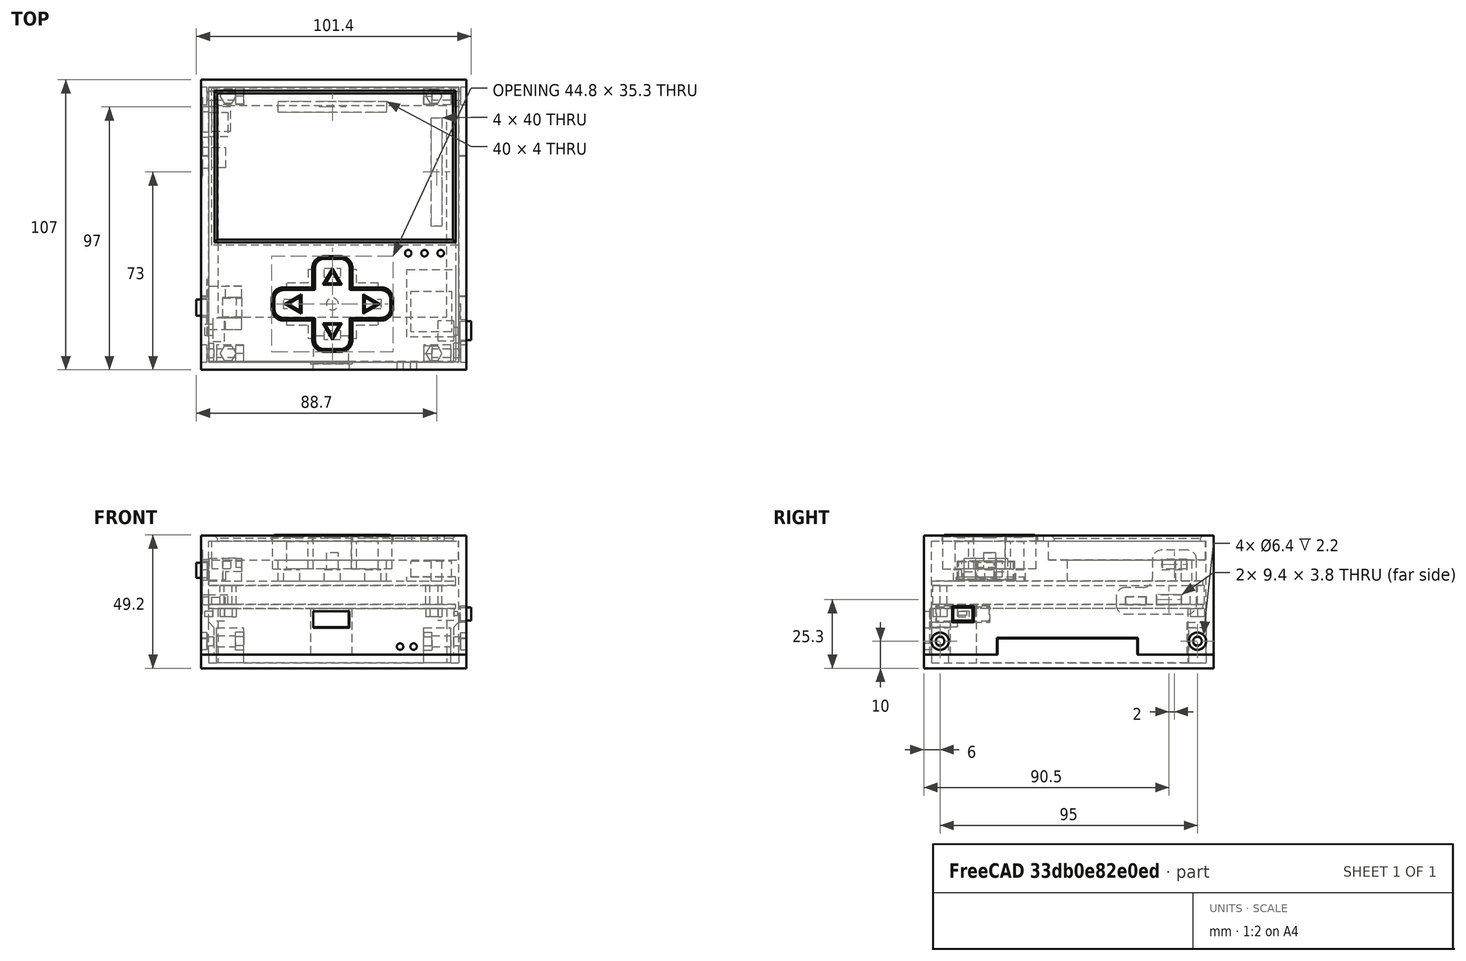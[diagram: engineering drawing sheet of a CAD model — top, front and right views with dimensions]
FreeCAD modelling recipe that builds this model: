
FCSTD DOCUMENT  (FreeCAD 0.19R24276 (Git))
Label: Cube-Vario
License: All rights reserved
LicenseURL: http://en.wikipedia.org/wiki/All_rights_reserved
objects: Sketcher::SketchObject×59, PartDesign::Pad×33, PartDesign::Pocket×23, PartDesign::ShapeBinder×8, PartDesign::Body×8, Mesh::Feature×6, PartDesign::Chamfer×3, PartDesign::Fillet×1
note: 195 computed .brp shape members not serialized (recipe doc carries the construction recipe); baked Part::Feature solids carry a one-line shape summary decoded from their .brp

FEATURE [Sketcher::SketchObject] Sketch
  FullyConstrained = true
  MapMode = 5
  Support = -> [XY_Plane]
  sketch-geometry (20):
    g0: LineSegment StartX=-45.5 StartY=50 StartZ=0 EndX=45.5 EndY=50 EndZ=0
    g1: LineSegment StartX=45.5 StartY=50 StartZ=0 EndX=45.5 EndY=-50 EndZ=0
    g2: LineSegment StartX=45.5 StartY=-50 StartZ=0 EndX=-45.5 EndY=-50 EndZ=0
    g3: LineSegment StartX=-45.5 StartY=-50 StartZ=0 EndX=-45.5 EndY=50 EndZ=0
    g4: LineSegment StartX=-42.2 StartY=44.4 StartZ=0 EndX=42.2 EndY=44.4 EndZ=0
    g5: LineSegment StartX=42.2 StartY=44.4 StartZ=0 EndX=42.2 EndY=-33.6 EndZ=0
    g6: LineSegment StartX=42.2 StartY=-33.6 StartZ=0 EndX=-42.2 EndY=-33.6 EndZ=0
    g7: LineSegment StartX=-42.2 StartY=-33.6 StartZ=0 EndX=-42.2 EndY=44.4 EndZ=0
    g8: LineSegment StartX=-44.1 StartY=-34 StartZ=0 EndX=-39.8 EndY=-34 EndZ=0
    g9: LineSegment StartX=-39.8 StartY=-34 StartZ=0 EndX=-39.8 EndY=-42.6 EndZ=0
    g10: LineSegment StartX=-39.8 StartY=-42.6 StartZ=0 EndX=-44.1 EndY=-42.6 EndZ=0
    g11: LineSegment StartX=-44.1 StartY=-42.6 StartZ=0 EndX=-44.1 EndY=-34 EndZ=0
    g12: LineSegment StartX=-7 StartY=-40.6 StartZ=0 EndX=6 EndY=-40.6 EndZ=0
    g13: LineSegment StartX=6 StartY=-40.6 StartZ=0 EndX=6 EndY=-50.6 EndZ=0
    g14: LineSegment StartX=6 StartY=-50.6 StartZ=0 EndX=-7 EndY=-50.6 EndZ=0
    g15: LineSegment StartX=-7 StartY=-50.6 StartZ=0 EndX=-7 EndY=-40.6 EndZ=0
    g16: LineSegment StartX=38.9 StartY=-35 StartZ=0 EndX=44.9 EndY=-35 EndZ=0
    g17: LineSegment StartX=44.9 StartY=-35 StartZ=0 EndX=44.9 EndY=-42.4 EndZ=0
    g18: LineSegment StartX=44.9 StartY=-42.4 StartZ=0 EndX=38.9 EndY=-42.4 EndZ=0
    g19: LineSegment StartX=38.9 StartY=-42.4 StartZ=0 EndX=38.9 EndY=-35 EndZ=0
  constraints (57):
    c: Coincident(g0,g1)
    c: Coincident(g1,g2)
    c: Coincident(g2,g3)
    c: Coincident(g3,g0)
    c: Horizontal(g2)
    c: Vertical(g3)
    c: DistanceX(g0,g0) = 91
    c: DistanceY(g3,g3) = 100
    c: Symmetric(g0,g0,g-2)
    c: Symmetric(g0,g1,g-1)
    c: Coincident(g4,g5)
    c: Coincident(g5,g6)
    c: Coincident(g6,g7)
    c: Coincident(g7,g4)
    c: Horizontal(g6)
    c: Vertical(g7)
    c: Coincident(g8,g9)
    c: Coincident(g9,g10)
    c: Coincident(g10,g11)
    c: Coincident(g11,g8)
    c: Horizontal(g8)
    c: Horizontal(g10)
    c: Vertical(g9)
    c: Vertical(g11)
    c: Coincident(g12,g13)
    c: Coincident(g13,g14)
    c: Coincident(g14,g15)
    c: Coincident(g15,g12)
    c: Horizontal(g12)
    c: Horizontal(g14)
    c: Vertical(g13)
    c: Vertical(g15)
    c: Coincident(g16,g17)
    c: Coincident(g17,g18)
    c: Coincident(g18,g19)
    c: Coincident(g19,g16)
    c: Horizontal(g16)
    c: Horizontal(g18)
    c: Vertical(g17)
    c: Vertical(g19)
    c: DistanceY(g4,g0) = 5.6
    c: DistanceY(g7,g7) = 78
    c: DistanceX(g4,g4) = 84.4
    c: Symmetric(g4,g4,g-2)
    c: Vertical(g5)
    c: DistanceY(g11,g11) = 8.6
    c: DistanceY(g17,g17) = 7.4
    c: DistanceX(g10,g10) = 4.3
    c: DistanceX(g14,g14) = 13
    c: DistanceY(g13,g13) = 10
    c: DistanceX(g2,g14) = 38.5
    c: DistanceX(g18,g18) = 6
    c: DistanceY(g1,g16) = 15
    c: DistanceY(g2,g8) = 16
    c: DistanceY(g13,g1) = 0.6
    c: DistanceX(g2,g10) = 1.4
    c: DistanceX(g18,g1) = 6.6
FEATURE [PartDesign::ShapeBinder] ShapeBinder
  Support = -> [Sketch]
  TraceSupport = false
FEATURE [Sketcher::SketchObject] Sketch001
  ExternalGeometry = -> [ShapeBinder]
  FullyConstrained = true
  MapMode = 5
  Support = -> [XY_Plane001]
  sketch-geometry (4):
    g0: LineSegment StartX=-45.5 StartY=50 StartZ=0 EndX=45.5 EndY=50 EndZ=0
    g1: LineSegment StartX=45.5 StartY=50 StartZ=0 EndX=45.5 EndY=-50 EndZ=0
    g2: LineSegment StartX=45.5 StartY=-50 StartZ=0 EndX=-45.5 EndY=-50 EndZ=0
    g3: LineSegment StartX=-45.5 StartY=-50 StartZ=0 EndX=-45.5 EndY=50 EndZ=0
  constraints (10):
    c: Coincident(g0,g1)
    c: Coincident(g1,g2)
    c: Coincident(g2,g3)
    c: Coincident(g3,g0)
    c: Horizontal(g0)
    c: Horizontal(g2)
    c: Vertical(g1)
    c: Vertical(g3)
    c: Coincident(g0,g-3)
    c: Coincident(g1,g-4)
FEATURE [PartDesign::Pad] Pad
  Direction = (1,1,1)
  Length = 1.6
  Length2 = 100
  Profile = -> Sketch001
  Type = 0
FEATURE [Sketcher::SketchObject] Sketch002
  ExternalGeometry = -> [ShapeBinder]
  FullyConstrained = true
  MapMode = 5
  Placement = pos=(0,0,0) rot=(1,0,0;3.14159rad)
  Support = -> [Pad]
  sketch-geometry (4):
    g0: LineSegment StartX=-42.2 StartY=33.6 StartZ=0 EndX=42.2 EndY=33.6 EndZ=0
    g1: LineSegment StartX=42.2 StartY=33.6 StartZ=0 EndX=42.2 EndY=-44.4 EndZ=0
    g2: LineSegment StartX=42.2 StartY=-44.4 StartZ=0 EndX=-42.2 EndY=-44.4 EndZ=0
    g3: LineSegment StartX=-42.2 StartY=-44.4 StartZ=0 EndX=-42.2 EndY=33.6 EndZ=0
  constraints (10):
    c: Coincident(g0,g1)
    c: Coincident(g1,g2)
    c: Coincident(g2,g3)
    c: Coincident(g3,g0)
    c: Horizontal(g0)
    c: Horizontal(g2)
    c: Vertical(g1)
    c: Vertical(g3)
    c: Coincident(g0,g-3)
    c: Coincident(g1,g-4)
FEATURE [PartDesign::Pad] Pad001
  BaseFeature = -> Pad
  Direction = (1,1,1)
  Length = 20
  Length2 = 100
  Profile = -> Sketch002
  Type = 0
FEATURE [Sketcher::SketchObject] Sketch003
  ExternalGeometry = -> [ShapeBinder]
  FullyConstrained = true
  MapMode = 5
  Placement = pos=(0,0,0) rot=(1,0,0;3.14159rad)
  Support = -> [Pad001]
  sketch-geometry (4):
    g0: LineSegment StartX=-7 StartY=50.6 StartZ=0 EndX=6 EndY=50.6 EndZ=0
    g1: LineSegment StartX=6 StartY=50.6 StartZ=0 EndX=6 EndY=40.6 EndZ=0
    g2: LineSegment StartX=6 StartY=40.6 StartZ=0 EndX=-7 EndY=40.6 EndZ=0
    g3: LineSegment StartX=-7 StartY=40.6 StartZ=0 EndX=-7 EndY=50.6 EndZ=0
  constraints (10):
    c: Coincident(g0,g1)
    c: Coincident(g1,g2)
    c: Coincident(g2,g3)
    c: Coincident(g3,g0)
    c: Horizontal(g0)
    c: Horizontal(g2)
    c: Vertical(g1)
    c: Vertical(g3)
    c: Coincident(g0,g-3)
    c: Coincident(g1,g-4)
FEATURE [PartDesign::Pad] Pad002
  BaseFeature = -> Pad001
  Direction = (1,1,1)
  Length = 6.8
  Length2 = 100
  Profile = -> Sketch003
  Type = 0
FEATURE [Sketcher::SketchObject] Sketch004
  ExternalGeometry = -> [ShapeBinder]
  FullyConstrained = true
  MapMode = 5
  Placement = pos=(0,0,0) rot=(1,0,0;3.14159rad)
  Support = -> [Pad002]
  sketch-geometry (4):
    g0: LineSegment StartX=-44.1 StartY=42.6 StartZ=0 EndX=-39.8 EndY=42.6 EndZ=0
    g1: LineSegment StartX=-39.8 StartY=42.6 StartZ=0 EndX=-39.8 EndY=34 EndZ=0
    g2: LineSegment StartX=-39.8 StartY=34 StartZ=0 EndX=-44.1 EndY=34 EndZ=0
    g3: LineSegment StartX=-44.1 StartY=34 StartZ=0 EndX=-44.1 EndY=42.6 EndZ=0
  constraints (10):
    c: Coincident(g0,g1)
    c: Coincident(g1,g2)
    c: Coincident(g2,g3)
    c: Coincident(g3,g0)
    c: Horizontal(g0)
    c: Horizontal(g2)
    c: Vertical(g1)
    c: Vertical(g3)
    c: Coincident(g0,g-3)
    c: Coincident(g1,g-4)
FEATURE [PartDesign::Pad] Pad003
  BaseFeature = -> Pad002
  Direction = (1,1,1)
  Length = 4.6
  Length2 = 100
  Profile = -> Sketch004
  Type = 0
FEATURE [Sketcher::SketchObject] Sketch005
  ExternalGeometry = -> [ShapeBinder]
  FullyConstrained = true
  MapMode = 5
  Placement = pos=(0,0,0) rot=(1,0,0;3.14159rad)
  Support = -> [Pad003]
  sketch-geometry (4):
    g0: LineSegment StartX=38.9 StartY=42.4 StartZ=0 EndX=44.9 EndY=42.4 EndZ=0
    g1: LineSegment StartX=44.9 StartY=42.4 StartZ=0 EndX=44.9 EndY=35 EndZ=0
    g2: LineSegment StartX=44.9 StartY=35 StartZ=0 EndX=38.9 EndY=35 EndZ=0
    g3: LineSegment StartX=38.9 StartY=35 StartZ=0 EndX=38.9 EndY=42.4 EndZ=0
  constraints (10):
    c: Coincident(g0,g1)
    c: Coincident(g1,g2)
    c: Coincident(g2,g3)
    c: Coincident(g3,g0)
    c: Horizontal(g0)
    c: Horizontal(g2)
    c: Vertical(g1)
    c: Vertical(g3)
    c: Coincident(g0,g-3)
    c: Coincident(g1,g-4)
FEATURE [PartDesign::Pad] Pad004
  BaseFeature = -> Pad003
  Direction = (1,1,1)
  Length = 4.4
  Length2 = 100
  Profile = -> Sketch005
  Type = 0
FEATURE [Sketcher::SketchObject] Sketch006
  ExternalGeometry = -> [Pad004]
  FullyConstrained = true
  MapMode = 5
  Placement = pos=(-44.1,0,0) rot=(0.57735,-0.57735,-0.57735;2.0944rad)
  Support = -> [Pad004]
  sketch-geometry (4):
    g0: LineSegment StartX=36.2 StartY=-1 StartZ=0 EndX=40.4 EndY=-1 EndZ=0
    g1: LineSegment StartX=40.4 StartY=-1 StartZ=0 EndX=40.4 EndY=-3 EndZ=0
    g2: LineSegment StartX=40.4 StartY=-3 StartZ=0 EndX=36.2 EndY=-3 EndZ=0
    g3: LineSegment StartX=36.2 StartY=-3 StartZ=0 EndX=36.2 EndY=-1 EndZ=0
  constraints (12):
    c: Coincident(g0,g1)
    c: Coincident(g1,g2)
    c: Coincident(g2,g3)
    c: Coincident(g3,g0)
    c: Horizontal(g0)
    c: Horizontal(g2)
    c: Vertical(g1)
    c: Vertical(g3)
    c: DistanceX(g0,g-4) = 2.2
    c: DistanceY(g3,g3) = 2
    c: DistanceX(g0,g0) = 4.2
    c: DistanceY(g0,g-3) = 1
FEATURE [PartDesign::Pad] Pad005
  BaseFeature = -> Pad004
  Direction = (1,1,1)
  Length = 3
  Length2 = 100
  Profile = -> Sketch006
  Type = 0
FEATURE [Sketcher::SketchObject] Sketch007
  ExternalGeometry = -> [Pad005]
  FullyConstrained = true
  MapMode = 5
  Placement = pos=(44.9,0,0) rot=(0.57735,0.57735,0.57735;2.0944rad)
  Support = -> [Pad005]
  sketch-geometry (4):
    g0: LineSegment StartX=-40.2 StartY=-1 StartZ=0 EndX=-37.2 EndY=-1 EndZ=0
    g1: LineSegment StartX=-37.2 StartY=-1 StartZ=0 EndX=-37.2 EndY=-2.5 EndZ=0
    g2: LineSegment StartX=-37.2 StartY=-2.5 StartZ=0 EndX=-40.2 EndY=-2.5 EndZ=0
    g3: LineSegment StartX=-40.2 StartY=-2.5 StartZ=0 EndX=-40.2 EndY=-1 EndZ=0
  constraints (12):
    c: Coincident(g0,g1)
    c: Coincident(g1,g2)
    c: Coincident(g2,g3)
    c: Coincident(g3,g0)
    c: Horizontal(g0)
    c: Horizontal(g2)
    c: Vertical(g1)
    c: Vertical(g3)
    c: DistanceX(g0,g0) = 3
    c: DistanceX(g0,g-4) = 2.2
    c: DistanceY(g3,g3) = 1.5
    c: DistanceY(g0,g-3) = 1
FEATURE [PartDesign::Pad] Pad006
  BaseFeature = -> Pad005
  Direction = (1,1,1)
  Length = 1.4
  Length2 = 100
  Profile = -> Sketch007
  Type = 0
FEATURE [Sketcher::SketchObject] Sketch008
  ExternalGeometry = -> [Pad006]
  FullyConstrained = true
  MapMode = 5
  Placement = pos=(0,0,1.6) rot=(0,0,1;0rad)
  Support = -> [Pad006]
  sketch-geometry (28):
    g0: LineSegment StartX=-40 StartY=45.4019 StartZ=0 EndX=-37 EndY=45.4019 EndZ=0
    g1: LineSegment StartX=-37 StartY=45.4019 StartZ=0 EndX=-35.5 EndY=48 EndZ=0
    g2: LineSegment StartX=-35.5 StartY=48 StartZ=0 EndX=-37 EndY=50.5981 EndZ=0
    g3: LineSegment StartX=-37 StartY=50.5981 StartZ=0 EndX=-40 EndY=50.5981 EndZ=0
    g4: LineSegment StartX=-40 StartY=50.5981 StartZ=0 EndX=-41.5 EndY=48 EndZ=0
    g5: LineSegment StartX=-41.5 StartY=48 StartZ=0 EndX=-40 EndY=45.4019 EndZ=0
    g6: Circle CenterX=-38.5 CenterY=48 CenterZ=0 NormalX=0 NormalY=0 NormalZ=1 AngleXU=0 Radius=3
    g7: LineSegment StartX=39 StartY=45.4019 StartZ=0 EndX=40.5 EndY=48 EndZ=0
    g8: LineSegment StartX=40.5 StartY=48 StartZ=0 EndX=39 EndY=50.5981 EndZ=0
    g9: LineSegment StartX=39 StartY=50.5981 StartZ=0 EndX=36 EndY=50.5981 EndZ=0
    g10: LineSegment StartX=36 StartY=50.5981 StartZ=0 EndX=34.5 EndY=48 EndZ=0
    g11: LineSegment StartX=34.5 StartY=48 StartZ=0 EndX=36 EndY=45.4019 EndZ=0
    g12: LineSegment StartX=36 StartY=45.4019 StartZ=0 EndX=39 EndY=45.4019 EndZ=0
    g13: Circle CenterX=37.5 CenterY=48 CenterZ=0 NormalX=0 NormalY=0 NormalZ=1 AngleXU=0 Radius=3
    g14: LineSegment StartX=-37 StartY=-49.5981 StartZ=0 EndX=-35.5 EndY=-47 EndZ=0
    g15: LineSegment StartX=-35.5 StartY=-47 StartZ=0 EndX=-37 EndY=-44.4019 EndZ=0
    g16: LineSegment StartX=-37 StartY=-44.4019 StartZ=0 EndX=-40 EndY=-44.4019 EndZ=0
    g17: LineSegment StartX=-40 StartY=-44.4019 StartZ=0 EndX=-41.5 EndY=-47 EndZ=0
    g18: LineSegment StartX=-41.5 StartY=-47 StartZ=0 EndX=-40 EndY=-49.5981 EndZ=0
    g19: LineSegment StartX=-40 StartY=-49.5981 StartZ=0 EndX=-37 EndY=-49.5981 EndZ=0
    g20: Circle CenterX=-38.5 CenterY=-47 CenterZ=0 NormalX=0 NormalY=0 NormalZ=1 AngleXU=0 Radius=3
    g21: LineSegment StartX=39 StartY=-49.5981 StartZ=0 EndX=40.5 EndY=-47 EndZ=0
    g22: LineSegment StartX=40.5 StartY=-47 StartZ=0 EndX=39 EndY=-44.4019 EndZ=0
    g23: LineSegment StartX=39 StartY=-44.4019 StartZ=0 EndX=36 EndY=-44.4019 EndZ=0
    g24: LineSegment StartX=36 StartY=-44.4019 StartZ=0 EndX=34.5 EndY=-47 EndZ=0
    g25: LineSegment StartX=34.5 StartY=-47 StartZ=0 EndX=36 EndY=-49.5981 EndZ=0
    g26: LineSegment StartX=36 StartY=-49.5981 StartZ=0 EndX=39 EndY=-49.5981 EndZ=0
    g27: Circle CenterX=37.5 CenterY=-47 CenterZ=0 NormalX=0 NormalY=0 NormalZ=1 AngleXU=0 Radius=3
  constraints (68):
    c: Coincident(g0,g1)
    c: Coincident(g1,g2)
    c: Coincident(g2,g3)
    c: Coincident(g3,g4)
    c: Coincident(g4,g5)
    c: Coincident(g5,g0)
    c: Equal(g0, g1-g5) x5
    c: PointOnObject(g0,g6)
    c: PointOnObject(g1,g6)
    c: PointOnObject(g2,g6)
    c: PointOnObject(g3,g6)
    c: PointOnObject(g4,g6)
    c: PointOnObject(g5,g6)
    c: Coincident(g7,g8)
    c: Coincident(g8,g9)
    c: Coincident(g9,g10)
    c: Coincident(g10,g11)
    c: Coincident(g11,g12)
    c: Coincident(g12,g7)
    c: Equal(g7, g8-g12) x5
    c: PointOnObject(g7,g13)
    c: PointOnObject(g8,g13)
    c: PointOnObject(g9,g13)
    c: PointOnObject(g10,g13)
    c: PointOnObject(g11,g13)
    c: PointOnObject(g12,g13)
    c: Coincident(g14,g15)
    c: Coincident(g15,g16)
    c: Coincident(g16,g17)
    c: Coincident(g17,g18)
    c: Coincident(g18,g19)
    c: Coincident(g19,g14)
    c: Equal(g14, g15-g19) x5
    c: PointOnObject(g14,g20)
    c: PointOnObject(g15,g20)
    c: PointOnObject(g16,g20)
    c: PointOnObject(g17,g20)
    c: PointOnObject(g18,g20)
    c: PointOnObject(g19,g20)
    c: Coincident(g21,g22)
    c: Coincident(g22,g23)
    c: Coincident(g23,g24)
    c: Coincident(g24,g25)
    c: Coincident(g25,g26)
    c: Coincident(g26,g21)
    c: Equal(g21, g22-g26) x5
    c: PointOnObject(g21,g27)
    c: PointOnObject(g22,g27)
    c: PointOnObject(g23,g27)
    c: PointOnObject(g24,g27)
    c: PointOnObject(g25,g27)
    c: PointOnObject(g26,g27)
    c: Equal(g20,g27)
    c: Radius(g27) = 3
    c: Horizontal(g17,g14)
    c: Horizontal(g24,g21)
    c: Horizontal(g4,g1)
    c: Horizontal(g10,g7)
    c: Equal(g20,g6)
    c: Equal(g6,g13)
    c: Horizontal(g6,g13)
    c: Horizontal(g20,g27)
    c: DistanceY(g6,g-3) = 2
    c: DistanceY(g-3,g20) = 3
    c: Vertical(g6,g20)
    c: DistanceX(g-3,g6) = 7
    c: Vertical(g13,g27)
    c: DistanceX(g13,g-4) = 8
FEATURE [PartDesign::Pad] Pad007
  BaseFeature = -> Pad006
  Direction = (1,1,1)
  Length = 7
  Length2 = 100
  Profile = -> Sketch008
  Type = 0
FEATURE [Sketcher::SketchObject] Sketch009
  ExternalGeometry = -> [Pad007]
  FullyConstrained = true
  MapMode = 5
  Placement = pos=(0,0,1.6) rot=(0,0,1;0rad)
  Support = -> [Pad007]
  sketch-geometry (4):
    g0: LineSegment StartX=-45.5 StartY=42 StartZ=0 EndX=-38.5 EndY=42 EndZ=0
    g1: LineSegment StartX=-38.5 StartY=42 StartZ=0 EndX=-38.5 EndY=33 EndZ=0
    g2: LineSegment StartX=-38.5 StartY=33 StartZ=0 EndX=-45.5 EndY=33 EndZ=0
    g3: LineSegment StartX=-45.5 StartY=33 StartZ=0 EndX=-45.5 EndY=42 EndZ=0
  constraints (12):
    c: Coincident(g0,g1)
    c: Coincident(g1,g2)
    c: Coincident(g2,g3)
    c: Coincident(g3,g0)
    c: Horizontal(g0)
    c: Horizontal(g2)
    c: Vertical(g1)
    c: Vertical(g3)
    c: PointOnObject(g0,g-3)
    c: DistanceX(g0,g0) = 7
    c: DistanceY(g3,g3) = 9
    c: DistanceY(g0,g-3) = 8
FEATURE [PartDesign::Pad] Pad008
  BaseFeature = -> Pad007
  Direction = (1,1,1)
  Length = 3.4
  Length2 = 100
  Profile = -> Sketch009
  Type = 0
FEATURE [Sketcher::SketchObject] Sketch010
  ExternalGeometry = -> [Pad008]
  FullyConstrained = true
  MapMode = 5
  Placement = pos=(0,0,1.6) rot=(0,0,1;0rad)
  Support = -> [Pad008]
  sketch-geometry (4):
    g0: LineSegment StartX=-44.5 StartY=29 StartZ=0 EndX=-39.5 EndY=29 EndZ=0
    g1: LineSegment StartX=-39.5 StartY=29 StartZ=0 EndX=-39.5 EndY=21.6 EndZ=0
    g2: LineSegment StartX=-39.5 StartY=21.6 StartZ=0 EndX=-44.5 EndY=21.6 EndZ=0
    g3: LineSegment StartX=-44.5 StartY=21.6 StartZ=0 EndX=-44.5 EndY=29 EndZ=0
  constraints (12):
    c: Coincident(g0,g1)
    c: Coincident(g1,g2)
    c: Coincident(g2,g3)
    c: Coincident(g3,g0)
    c: Horizontal(g0)
    c: Horizontal(g2)
    c: Vertical(g1)
    c: Vertical(g3)
    c: DistanceX(g0,g0) = 5
    c: DistanceY(g3,g3) = 7.4
    c: DistanceY(g0,g-4) = 21
    c: DistanceX(g-4,g0) = 1
FEATURE [PartDesign::Pad] Pad009
  BaseFeature = -> Pad008
  Direction = (1,1,1)
  Length = 2.6
  Length2 = 100
  Profile = -> Sketch010
  Type = 0
FEATURE [Sketcher::SketchObject] Sketch011
  ExternalGeometry = -> [Pad009]
  FullyConstrained = true
  MapMode = 5
  Placement = pos=(0,0,8.6) rot=(0,0,1;0rad)
  Support = -> [Pad009]
  sketch-geometry (4):
    g0: LineSegment StartX=-45.5 StartY=50 StartZ=0 EndX=45.5 EndY=50 EndZ=0
    g1: LineSegment StartX=45.5 StartY=50 StartZ=0 EndX=45.5 EndY=-50 EndZ=0
    g2: LineSegment StartX=45.5 StartY=-50 StartZ=0 EndX=-45.5 EndY=-50 EndZ=0
    g3: LineSegment StartX=-45.5 StartY=-50 StartZ=0 EndX=-45.5 EndY=50 EndZ=0
  constraints (10):
    c: Coincident(g0,g1)
    c: Coincident(g1,g2)
    c: Coincident(g2,g3)
    c: Coincident(g3,g0)
    c: Horizontal(g0)
    c: Horizontal(g2)
    c: Vertical(g1)
    c: Vertical(g3)
    c: Coincident(g0,g-3)
    c: Coincident(g1,g-4)
FEATURE [PartDesign::Pad] Pad010
  BaseFeature = -> Pad009
  Direction = (1,1,1)
  Length = 1.6
  Length2 = 100
  Profile = -> Sketch011
  Type = 0
FEATURE [Sketcher::SketchObject] Sketch012
  ExternalGeometry = -> [Pad010]
  FullyConstrained = true
  MapMode = 5
  Placement = pos=(0,0,10.2) rot=(0,0,1;0rad)
  Support = -> [Pad010]
  sketch-geometry (8):
    g0: LineSegment StartX=-20 StartY=46 StartZ=0 EndX=20 EndY=46 EndZ=0
    g1: LineSegment StartX=20 StartY=46 StartZ=0 EndX=20 EndY=42 EndZ=0
    g2: LineSegment StartX=20 StartY=42 StartZ=0 EndX=-20 EndY=42 EndZ=0
    g3: LineSegment StartX=-20 StartY=42 StartZ=0 EndX=-20 EndY=46 EndZ=0
    g4: LineSegment StartX=36.5 StartY=40 StartZ=0 EndX=40.5 EndY=40 EndZ=0
    g5: LineSegment StartX=40.5 StartY=40 StartZ=0 EndX=40.5 EndY=5.1941e-12 EndZ=0
    g6: LineSegment StartX=40.5 StartY=5.1941e-12 StartZ=0 EndX=36.5 EndY=5.1941e-12 EndZ=0
    g7: LineSegment StartX=36.5 StartY=5.1941e-12 StartZ=0 EndX=36.5 EndY=40 EndZ=0
  constraints (23):
    c: Coincident(g0,g1)
    c: Coincident(g1,g2)
    c: Coincident(g2,g3)
    c: Coincident(g3,g0)
    c: Horizontal(g2)
    c: Vertical(g1)
    c: Vertical(g3)
    c: Coincident(g4,g5)
    c: Coincident(g5,g6)
    c: Coincident(g6,g7)
    c: Coincident(g7,g4)
    c: Horizontal(g4)
    c: Horizontal(g6)
    c: Vertical(g5)
    c: Vertical(g7)
    c: Equal(g1,g4)
    c: Equal(g2,g7)
    c: Symmetric(g0,g0,g-2)
    c: DistanceX(g0,g0) = 40
    c: DistanceY(g3,g3) = 4
    c: DistanceX(g4,g-3) = 5
    c: DistanceY(g4,g2) = 2
    c: DistanceY(g0,g-3) = 4
FEATURE [PartDesign::Pad] Pad011
  BaseFeature = -> Pad010
  Direction = (1,1,1)
  Length = 7.8
  Length2 = 100
  Profile = -> Sketch012
  Type = 0
FEATURE [Sketcher::SketchObject] Sketch013
  ExternalGeometry = -> [Pad011]
  FullyConstrained = true
  MapMode = 5
  Placement = pos=(0,0,18) rot=(0,0,1;0rad)
  Support = -> [Pad011]
  sketch-geometry (4):
    g0: LineSegment StartX=-44.5 StartY=51 StartZ=0 EndX=46.5 EndY=51 EndZ=0
    g1: LineSegment StartX=46.5 StartY=51 StartZ=0 EndX=46.5 EndY=-7 EndZ=0
    g2: LineSegment StartX=46.5 StartY=-7 StartZ=0 EndX=-44.5 EndY=-7 EndZ=0
    g3: LineSegment StartX=-44.5 StartY=-7 StartZ=0 EndX=-44.5 EndY=51 EndZ=0
  constraints (12):
    c: Coincident(g0,g1)
    c: Coincident(g1,g2)
    c: Coincident(g2,g3)
    c: Coincident(g3,g0)
    c: Horizontal(g0)
    c: Horizontal(g2)
    c: Vertical(g1)
    c: Vertical(g3)
    c: DistanceY(g3,g3) = 58
    c: DistanceX(g0,g0) = 91
    c: DistanceX(g-3,g0) = 1
    c: DistanceY(g-3,g0) = 1
FEATURE [PartDesign::Pad] Pad012
  BaseFeature = -> Pad011
  Direction = (1,1,1)
  Length = 7
  Length2 = 100
  Profile = -> Sketch013
  Type = 0
FEATURE [Sketcher::SketchObject] Sketch014
  ExternalGeometry = -> [Pad012]
  FullyConstrained = true
  MapMode = 5
  Placement = pos=(0,0,18) rot=(1,0,0;3.14159rad)
  Support = -> [Pad012]
  sketch-geometry (4):
    g0: LineSegment StartX=-44.5 StartY=-35 StartZ=0 EndX=-37.5 EndY=-35 EndZ=0
    g1: LineSegment StartX=-37.5 StartY=-35 StartZ=0 EndX=-37.5 EndY=-44 EndZ=0
    g2: LineSegment StartX=-37.5 StartY=-44 StartZ=0 EndX=-44.5 EndY=-44 EndZ=0
    g3: LineSegment StartX=-44.5 StartY=-44 StartZ=0 EndX=-44.5 EndY=-35 EndZ=0
  constraints (12):
    c: Coincident(g0,g1)
    c: Coincident(g1,g2)
    c: Coincident(g2,g3)
    c: Coincident(g3,g0)
    c: Horizontal(g0)
    c: Horizontal(g2)
    c: Vertical(g1)
    c: Vertical(g3)
    c: PointOnObject(g0,g-3)
    c: DistanceX(g0,g0) = 7
    c: DistanceY(g3,g3) = 9
    c: DistanceY(g-3,g2) = 7
FEATURE [PartDesign::Pad] Pad013
  BaseFeature = -> Pad012
  Direction = (1,1,1)
  Length = 3.4
  Length2 = 100
  Profile = -> Sketch014
  Type = 0
FEATURE [Sketcher::SketchObject] Sketch015
  ExternalGeometry = -> [Pad013]
  FullyConstrained = true
  MapMode = 5
  Placement = pos=(0,0,0) rot=(1,0,0;3.14159rad)
  Support = -> [Pad013]
  sketch-geometry (28):
    g0: LineSegment StartX=-35.5 StartY=47 StartZ=0 EndX=-37 EndY=49.5981 EndZ=0
    g1: LineSegment StartX=-37 StartY=49.5981 StartZ=0 EndX=-40 EndY=49.5981 EndZ=0
    g2: LineSegment StartX=-40 StartY=49.5981 StartZ=0 EndX=-41.5 EndY=47 EndZ=0
    g3: LineSegment StartX=-41.5 StartY=47 StartZ=0 EndX=-40 EndY=44.4019 EndZ=0
    g4: LineSegment StartX=-40 StartY=44.4019 StartZ=0 EndX=-37 EndY=44.4019 EndZ=0
    g5: LineSegment StartX=-37 StartY=44.4019 StartZ=0 EndX=-35.5 EndY=47 EndZ=0
    g6: Circle CenterX=-38.5 CenterY=47 CenterZ=0 NormalX=0 NormalY=0 NormalZ=1 AngleXU=0 Radius=3
    g7: LineSegment StartX=39 StartY=44.4019 StartZ=0 EndX=40.5 EndY=47 EndZ=0
    g8: LineSegment StartX=40.5 StartY=47 StartZ=0 EndX=39 EndY=49.5981 EndZ=0
    g9: LineSegment StartX=39 StartY=49.5981 StartZ=0 EndX=36 EndY=49.5981 EndZ=0
    g10: LineSegment StartX=36 StartY=49.5981 StartZ=0 EndX=34.5 EndY=47 EndZ=0
    g11: LineSegment StartX=34.5 StartY=47 StartZ=0 EndX=36 EndY=44.4019 EndZ=0
    g12: LineSegment StartX=36 StartY=44.4019 StartZ=0 EndX=39 EndY=44.4019 EndZ=0
    g13: Circle CenterX=37.5 CenterY=47 CenterZ=0 NormalX=0 NormalY=0 NormalZ=1 AngleXU=0 Radius=3
    g14: LineSegment StartX=-37 StartY=-50.5981 StartZ=0 EndX=-35.5 EndY=-48 EndZ=0
    g15: LineSegment StartX=-35.5 StartY=-48 StartZ=0 EndX=-37 EndY=-45.4019 EndZ=0
    g16: LineSegment StartX=-37 StartY=-45.4019 StartZ=0 EndX=-40 EndY=-45.4019 EndZ=0
    g17: LineSegment StartX=-40 StartY=-45.4019 StartZ=0 EndX=-41.5 EndY=-48 EndZ=0
    g18: LineSegment StartX=-41.5 StartY=-48 StartZ=0 EndX=-40 EndY=-50.5981 EndZ=0
    g19: LineSegment StartX=-40 StartY=-50.5981 StartZ=0 EndX=-37 EndY=-50.5981 EndZ=0
    g20: Circle CenterX=-38.5 CenterY=-48 CenterZ=0 NormalX=0 NormalY=0 NormalZ=1 AngleXU=0 Radius=3
    g21: LineSegment StartX=39 StartY=-50.5981 StartZ=0 EndX=40.5 EndY=-48 EndZ=0
    g22: LineSegment StartX=40.5 StartY=-48 StartZ=0 EndX=39 EndY=-45.4019 EndZ=0
    g23: LineSegment StartX=39 StartY=-45.4019 StartZ=0 EndX=36 EndY=-45.4019 EndZ=0
    g24: LineSegment StartX=36 StartY=-45.4019 StartZ=0 EndX=34.5 EndY=-48 EndZ=0
    g25: LineSegment StartX=34.5 StartY=-48 StartZ=0 EndX=36 EndY=-50.5981 EndZ=0
    g26: LineSegment StartX=36 StartY=-50.5981 StartZ=0 EndX=39 EndY=-50.5981 EndZ=0
    g27: Circle CenterX=37.5 CenterY=-48 CenterZ=0 NormalX=0 NormalY=0 NormalZ=1 AngleXU=0 Radius=3
  constraints (64):
    c: Coincident(g0,g1)
    c: Coincident(g1,g2)
    c: Coincident(g2,g3)
    c: Coincident(g3,g4)
    c: Coincident(g4,g5)
    c: Coincident(g5,g0)
    c: Equal(g0, g1-g5) x5
    c: PointOnObject(g0,g6)
    c: PointOnObject(g1,g6)
    c: PointOnObject(g2,g6)
    c: PointOnObject(g3,g6)
    c: PointOnObject(g4,g6)
    c: PointOnObject(g5,g6)
    c: Coincident(g7,g8)
    c: Coincident(g8,g9)
    c: Coincident(g9,g10)
    c: Coincident(g10,g11)
    c: Coincident(g11,g12)
    c: Coincident(g12,g7)
    c: Equal(g7, g8-g12) x5
    c: PointOnObject(g7,g13)
    c: PointOnObject(g8,g13)
    c: PointOnObject(g9,g13)
    c: PointOnObject(g10,g13)
    c: PointOnObject(g11,g13)
    c: PointOnObject(g12,g13)
    c: Coincident(g14,g15)
    c: Coincident(g15,g16)
    c: Coincident(g16,g17)
    c: Coincident(g17,g18)
    c: Coincident(g18,g19)
    c: Coincident(g19,g14)
    c: Equal(g14, g15-g19) x5
    c: PointOnObject(g14,g20)
    c: PointOnObject(g15,g20)
    c: PointOnObject(g16,g20)
    c: PointOnObject(g17,g20)
    c: PointOnObject(g18,g20)
    c: PointOnObject(g19,g20)
    c: Coincident(g21,g22)
    c: Coincident(g22,g23)
    c: Coincident(g23,g24)
    c: Coincident(g24,g25)
    c: Coincident(g25,g26)
    c: Coincident(g26,g21)
    c: Equal(g21, g22-g26) x5
    c: PointOnObject(g21,g27)
    c: PointOnObject(g22,g27)
    c: PointOnObject(g23,g27)
    c: PointOnObject(g24,g27)
    c: PointOnObject(g25,g27)
    c: PointOnObject(g26,g27)
    c: Equal(g6,g13)
    c: Equal(g13,g20)
    c: Equal(g20,g27)
    c: Radius(g27) = 3
    c: Horizontal(g21,g24)
    c: Coincident(g21,g-10)
    c: Horizontal(g14,g17)
    c: Coincident(g17,g-7)
    c: Horizontal(g0,g2)
    c: Coincident(g2,g-3)
    c: Horizontal(g10,g7)
    c: Coincident(g7,g-6)
FEATURE [PartDesign::Pad] Pad014
  BaseFeature = -> Pad013
  Direction = (1,1,1)
  Length = 3
  Length2 = 100
  Profile = -> Sketch015
  Type = 0
FEATURE [PartDesign::ShapeBinder] ShapeBinder001
  Support = -> [Sketch]
  TraceSupport = false
FEATURE [PartDesign::ShapeBinder] ShapeBinder002
  Support = -> [Sketch]
  TraceSupport = false
FEATURE [Sketcher::SketchObject] Sketch016
  FullyConstrained = true
  MapMode = 5
  Placement = pos=(0,0,0) rot=(0.57735,0.57735,0.57735;2.0944rad)
  Support = -> [YZ_Plane]
  sketch-geometry (14):
    g0: LineSegment StartX=-44.4019 StartY=-13.5 StartZ=0 EndX=-44.4019 EndY=-10.5 EndZ=0
    g1: LineSegment StartX=-44.4019 StartY=-10.5 StartZ=0 EndX=-47 EndY=-9 EndZ=0
    g2: LineSegment StartX=-47 StartY=-9 StartZ=0 EndX=-49.5981 EndY=-10.5 EndZ=0
    g3: LineSegment StartX=-49.5981 StartY=-10.5 StartZ=0 EndX=-49.5981 EndY=-13.5 EndZ=0
    g4: LineSegment StartX=-49.5981 StartY=-13.5 StartZ=0 EndX=-47 EndY=-15 EndZ=0
    g5: LineSegment StartX=-47 StartY=-15 StartZ=0 EndX=-44.4019 EndY=-13.5 EndZ=0
    g6: Circle CenterX=-47 CenterY=-12 CenterZ=0 NormalX=0 NormalY=0 NormalZ=1 AngleXU=0 Radius=3
    g7: LineSegment StartX=50.5981 StartY=-10.5 StartZ=0 EndX=48 EndY=-9 EndZ=0
    g8: LineSegment StartX=48 StartY=-9 StartZ=0 EndX=45.4019 EndY=-10.5 EndZ=0
    g9: LineSegment StartX=45.4019 StartY=-10.5 StartZ=0 EndX=45.4019 EndY=-13.5 EndZ=0
    g10: LineSegment StartX=45.4019 StartY=-13.5 StartZ=0 EndX=48 EndY=-15 EndZ=0
    g11: LineSegment StartX=48 StartY=-15 StartZ=0 EndX=50.5981 EndY=-13.5 EndZ=0
    g12: LineSegment StartX=50.5981 StartY=-13.5 StartZ=0 EndX=50.5981 EndY=-10.5 EndZ=0
    g13: Circle CenterX=48 CenterY=-12 CenterZ=0 NormalX=0 NormalY=0 NormalZ=1 AngleXU=0 Radius=3
  constraints (34):
    c: Coincident(g0,g1)
    c: Coincident(g1,g2)
    c: Coincident(g2,g3)
    c: Coincident(g3,g4)
    c: Coincident(g4,g5)
    c: Coincident(g5,g0)
    c: Equal(g0, g1-g5) x5
    c: PointOnObject(g0,g6)
    c: PointOnObject(g1,g6)
    c: PointOnObject(g2,g6)
    c: PointOnObject(g3,g6)
    c: PointOnObject(g4,g6)
    c: PointOnObject(g5,g6)
    c: Coincident(g7,g8)
    c: Coincident(g8,g9)
    c: Coincident(g9,g10)
    c: Coincident(g10,g11)
    c: Coincident(g11,g12)
    c: Coincident(g12,g7)
    c: Equal(g7, g8-g12) x5
    c: PointOnObject(g7,g13)
    c: PointOnObject(g8,g13)
    c: PointOnObject(g9,g13)
    c: PointOnObject(g10,g13)
    c: PointOnObject(g11,g13)
    c: PointOnObject(g12,g13)
    c: Equal(g6,g13)
    c: Radius(g13) = 3
    c: Vertical(g1,g4)
    c: Vertical(g10,g7)
    c: DistanceX(g-1,g13) = 48
    c: DistanceY(g6,g-1) = 12
    c: DistanceX(g6,g-1) = 47
    c: Horizontal(g6,g13)
FEATURE [PartDesign::ShapeBinder] ShapeBinder003
  Support = -> [Sketch016]
  TraceSupport = false
FEATURE [PartDesign::ShapeBinder] ShapeBinder004
  Support = -> [Sketch016,ShapeBinder003]
  TraceSupport = false
FEATURE [Sketcher::SketchObject] Sketch017
  AttachmentOffset = pos=(0,0,-22) rot=(0,0,1;0rad)
  ExternalGeometry = -> [ShapeBinder001]
  FullyConstrained = true
  MapMode = 5
  Placement = pos=(0,0,-22) rot=(0,0,1;0rad)
  Support = -> [XY_Plane002]
  sketch-geometry (4):
    g0: LineSegment StartX=-48.5 StartY=54 StartZ=0 EndX=49.5 EndY=54 EndZ=0
    g1: LineSegment StartX=49.5 StartY=54 StartZ=0 EndX=49.5 EndY=-53 EndZ=0
    g2: LineSegment StartX=49.5 StartY=-53 StartZ=0 EndX=-48.5 EndY=-53 EndZ=0
    g3: LineSegment StartX=-48.5 StartY=-53 StartZ=0 EndX=-48.5 EndY=54 EndZ=0
  constraints (12):
    c: Coincident(g0,g1)
    c: Coincident(g1,g2)
    c: Coincident(g2,g3)
    c: Coincident(g3,g0)
    c: Horizontal(g0)
    c: Horizontal(g2)
    c: Vertical(g1)
    c: Vertical(g3)
    c: DistanceX(g0,g-3) = 3
    c: DistanceX(g-5,g0) = 4
    c: DistanceY(g-3,g0) = 4
    c: DistanceY(g2,g-6) = 3
FEATURE [PartDesign::Pad] Pad015
  Direction = (1,1,1)
  Length = 5
  Length2 = 100
  Profile = -> Sketch017
  Type = 0
FEATURE [Sketcher::SketchObject] Sketch018
  ExternalGeometry = -> [ShapeBinder001]
  FullyConstrained = true
  MapMode = 5
  Placement = pos=(0,0,-17) rot=(0,0,1;0rad)
  Support = -> [Pad015]
  sketch-geometry (4):
    g0: LineSegment StartX=-45.7 StartY=51.2 StartZ=0 EndX=46.7 EndY=51.2 EndZ=0
    g1: LineSegment StartX=46.7 StartY=51.2 StartZ=0 EndX=46.7 EndY=-50.2 EndZ=0
    g2: LineSegment StartX=46.7 StartY=-50.2 StartZ=0 EndX=-45.7 EndY=-50.2 EndZ=0
    g3: LineSegment StartX=-45.7 StartY=-50.2 StartZ=0 EndX=-45.7 EndY=51.2 EndZ=0
  constraints (12):
    c: Coincident(g0,g1)
    c: Coincident(g1,g2)
    c: Coincident(g2,g3)
    c: Coincident(g3,g0)
    c: Horizontal(g0)
    c: Horizontal(g2)
    c: Vertical(g1)
    c: Vertical(g3)
    c: DistanceX(g0,g-3) = 0.2
    c: DistanceY(g-3,g0) = 1.2
    c: DistanceX(g-4,g1) = 1.2
    c: DistanceY(g1,g-4) = 0.2
FEATURE [PartDesign::Pocket] Pocket
  BaseFeature = -> Pad015
  Length = 3
  Length2 = 100
  Profile = -> Sketch018
  Type = 0
FEATURE [Sketcher::SketchObject] Sketch019
  ExternalGeometry = -> [Pocket]
  FullyConstrained = true
  MapMode = 5
  Placement = pos=(0,0,-17) rot=(0,0,1;0rad)
  Support = -> [Pocket]
  sketch-geometry (8):
    g0: LineSegment StartX=-48.5 StartY=25.8 StartZ=0 EndX=-45.7 EndY=25.8 EndZ=0
    g1: LineSegment StartX=-45.7 StartY=25.8 StartZ=0 EndX=-45.7 EndY=-25.8 EndZ=0
    g2: LineSegment StartX=-45.7 StartY=-25.8 StartZ=0 EndX=-48.5 EndY=-25.8 EndZ=0
    g3: LineSegment StartX=-48.5 StartY=-25.8 StartZ=0 EndX=-48.5 EndY=25.8 EndZ=0
    g4: LineSegment StartX=46.7 StartY=25.8 StartZ=0 EndX=49.5 EndY=25.8 EndZ=0
    g5: LineSegment StartX=49.5 StartY=25.8 StartZ=0 EndX=49.5 EndY=-25.8 EndZ=0
    g6: LineSegment StartX=49.5 StartY=-25.8 StartZ=0 EndX=46.7 EndY=-25.8 EndZ=0
    g7: LineSegment StartX=46.7 StartY=-25.8 StartZ=0 EndX=46.7 EndY=25.8 EndZ=0
  constraints (23):
    c: Coincident(g0,g1)
    c: Coincident(g1,g2)
    c: Coincident(g2,g3)
    c: Coincident(g3,g0)
    c: Horizontal(g0)
    c: Horizontal(g2)
    c: Vertical(g1)
    c: PointOnObject(g0,g-3)
    c: PointOnObject(g1,g-4)
    c: Coincident(g4,g5)
    c: Coincident(g5,g6)
    c: Coincident(g6,g7)
    c: Coincident(g7,g4)
    c: Horizontal(g4)
    c: Horizontal(g6)
    c: Vertical(g5)
    c: Vertical(g7)
    c: PointOnObject(g4,g-5)
    c: PointOnObject(g5,g-6)
    c: Equal(g1,g7)
    c: Horizontal(g0,g4)
    c: Symmetric(g0,g2,g-1)
    c: DistanceY(g-1,g0) = 25.8
FEATURE [PartDesign::Pad] Pad016
  BaseFeature = -> Pocket
  Direction = (1,1,1)
  Length = 6
  Length2 = 100
  Profile = -> Sketch019
  Type = 0
FEATURE [Sketcher::SketchObject] Sketch020
  ExternalGeometry = -> [Pad016]
  FullyConstrained = true
  MapMode = 5
  Placement = pos=(0,0,-20) rot=(0,0,1;0rad)
  Support = -> [Pad016]
  sketch-geometry (16):
    g0: LineSegment StartX=-42.7 StartY=51.2 StartZ=0 EndX=-32.7 EndY=51.2 EndZ=0
    g1: LineSegment StartX=-32.7 StartY=51.2 StartZ=0 EndX=-32.7 EndY=44.8 EndZ=0
    g2: LineSegment StartX=-32.7 StartY=44.8 StartZ=0 EndX=-42.7 EndY=44.8 EndZ=0
    g3: LineSegment StartX=-42.7 StartY=44.8 StartZ=0 EndX=-42.7 EndY=51.2 EndZ=0
    g4: LineSegment StartX=33.7 StartY=51.2 StartZ=0 EndX=43.7 EndY=51.2 EndZ=0
    g5: LineSegment StartX=43.7 StartY=51.2 StartZ=0 EndX=43.7 EndY=44.8 EndZ=0
    g6: LineSegment StartX=43.7 StartY=44.8 StartZ=0 EndX=33.7 EndY=44.8 EndZ=0
    g7: LineSegment StartX=33.7 StartY=44.8 StartZ=0 EndX=33.7 EndY=51.2 EndZ=0
    g8: LineSegment StartX=-42.7 StartY=-50.2 StartZ=0 EndX=-32.7 EndY=-50.2 EndZ=0
    g9: LineSegment StartX=-32.7 StartY=-50.2 StartZ=0 EndX=-32.7 EndY=-43.8 EndZ=0
    g10: LineSegment StartX=-32.7 StartY=-43.8 StartZ=0 EndX=-42.7 EndY=-43.8 EndZ=0
    g11: LineSegment StartX=-42.7 StartY=-43.8 StartZ=0 EndX=-42.7 EndY=-50.2 EndZ=0
    g12: LineSegment StartX=33.7 StartY=-50.2 StartZ=0 EndX=43.7 EndY=-50.2 EndZ=0
    g13: LineSegment StartX=43.7 StartY=-50.2 StartZ=0 EndX=43.7 EndY=-43.8 EndZ=0
    g14: LineSegment StartX=43.7 StartY=-43.8 StartZ=0 EndX=33.7 EndY=-43.8 EndZ=0
    g15: LineSegment StartX=33.7 StartY=-43.8 StartZ=0 EndX=33.7 EndY=-50.2 EndZ=0
  constraints (48):
    c: Coincident(g0,g1)
    c: Coincident(g1,g2)
    c: Coincident(g2,g3)
    c: Coincident(g3,g0)
    c: Horizontal(g0)
    c: Horizontal(g2)
    c: Vertical(g1)
    c: Vertical(g3)
    c: PointOnObject(g0,g-3)
    c: Coincident(g4,g5)
    c: Coincident(g5,g6)
    c: Coincident(g6,g7)
    c: Coincident(g7,g4)
    c: Horizontal(g4)
    c: Horizontal(g6)
    c: Vertical(g5)
    c: Vertical(g7)
    c: PointOnObject(g4,g-3)
    c: Coincident(g8,g9)
    c: Coincident(g9,g10)
    c: Coincident(g10,g11)
    c: Coincident(g11,g8)
    c: Horizontal(g8)
    c: Horizontal(g10)
    c: Vertical(g9)
    c: Vertical(g11)
    c: PointOnObject(g8,g-4)
    c: Coincident(g12,g13)
    c: Coincident(g13,g14)
    c: Coincident(g14,g15)
    c: Coincident(g15,g12)
    c: Horizontal(g12)
    c: Horizontal(g14)
    c: Vertical(g13)
    c: Vertical(g15)
    c: PointOnObject(g12,g-4)
    c: Equal(g2,g10)
    c: Equal(g10,g14)
    c: Equal(g14,g6)
    c: Equal(g1,g7)
    c: Equal(g7,g15)
    c: Equal(g15,g9)
    c: DistanceX(g0,g0) = 10
    c: DistanceY(g1,g1) = 6.4
    c: DistanceX(g-3,g0) = 3
    c: Vertical(g9,g1)
    c: Vertical(g14,g6)
    c: DistanceX(g4,g-3) = 3
FEATURE [PartDesign::Pad] Pad017
  BaseFeature = -> Pad016
  Direction = (1,1,1)
  Length = 13
  Length2 = 100
  Profile = -> Sketch020
  Type = 0
FEATURE [Sketcher::SketchObject] Sketch021
  ExternalGeometry = -> [ShapeBinder003]
  FullyConstrained = true
  MapMode = 5
  Placement = pos=(43.7,0,0) rot=(0.57735,0.57735,0.57735;2.0944rad)
  Support = -> [Pad017]
  sketch-geometry (8):
    g0: ArcOfCircle CenterX=-47 CenterY=-11.6 CenterZ=0 NormalX=0 NormalY=0 NormalZ=1 AngleXU=0 Radius=1.6 StartAngle=0 EndAngle=3.14159
    g1: ArcOfCircle CenterX=-47 CenterY=-12.4 CenterZ=0 NormalX=0 NormalY=0 NormalZ=1 AngleXU=0 Radius=1.6 StartAngle=3.14159 EndAngle=6.28319
    g2: LineSegment StartX=-48.6 StartY=-11.6 StartZ=0 EndX=-48.6 EndY=-12.4 EndZ=0
    g3: LineSegment StartX=-45.4 StartY=-11.6 StartZ=0 EndX=-45.4 EndY=-12.4 EndZ=0
    g4: ArcOfCircle CenterX=48 CenterY=-11.6 CenterZ=0 NormalX=0 NormalY=0 NormalZ=1 AngleXU=0 Radius=1.6 StartAngle=4e-16 EndAngle=3.14159
    g5: ArcOfCircle CenterX=48 CenterY=-12.4 CenterZ=0 NormalX=0 NormalY=0 NormalZ=1 AngleXU=0 Radius=1.6 StartAngle=3.14159 EndAngle=6.28319
    g6: LineSegment StartX=46.4 StartY=-11.6 StartZ=0 EndX=46.4 EndY=-12.4 EndZ=0
    g7: LineSegment StartX=49.6 StartY=-11.6 StartZ=0 EndX=49.6 EndY=-12.4 EndZ=0
  constraints (21):
    c: Tangent(g0,g3) = 1.5708
    c: Tangent(g0,g2) = -1.5708
    c: Tangent(g2,g1) = -1.5708
    c: Tangent(g3,g1) = 1.5708
    c: Equal(g0,g1)
    c: Tangent(g4,g7) = 1.5708
    c: Tangent(g4,g6) = -1.5708
    c: Tangent(g6,g5) = -1.5708
    c: Tangent(g7,g5) = 1.5708
    c: Equal(g4,g5)
    c: Equal(g0,g4)
    c: Radius(g1) = 1.6
    c: Vertical(g0,g1)
    c: Vertical(g1,g-3)
    c: DistanceY(g1,g0) = 0.8
    c: DistanceY(g5,g4) = 0.8
    c: Vertical(g5,g4)
    c: Vertical(g4,g-5)
    c: DistanceY(g-4,g-3) = 6
    c: DistanceY(g0,g-3) = 2.6
    c: DistanceY(g4,g-5) = 2.6
FEATURE [PartDesign::Pocket] Pocket001
  BaseFeature = -> Pad017
  Length = 5
  Length2 = 100
  Profile = -> Sketch021
  Type = 1
FEATURE [Sketcher::SketchObject] Sketch023
  AttachmentOffset = pos=(0,0,27) rot=(0,0,1;0rad)
  ExternalGeometry = -> [ShapeBinder002]
  FullyConstrained = true
  MapMode = 5
  Placement = pos=(0,0,27) rot=(0,0,1;0rad)
  Support = -> [XY_Plane003]
  sketch-geometry (4):
    g0: LineSegment StartX=-48.5 StartY=54 StartZ=0 EndX=49.5 EndY=54 EndZ=0
    g1: LineSegment StartX=49.5 StartY=54 StartZ=0 EndX=49.5 EndY=-53 EndZ=0
    g2: LineSegment StartX=49.5 StartY=-53 StartZ=0 EndX=-48.5 EndY=-53 EndZ=0
    g3: LineSegment StartX=-48.5 StartY=-53 StartZ=0 EndX=-48.5 EndY=54 EndZ=0
  constraints (12):
    c: Coincident(g0,g1)
    c: Coincident(g1,g2)
    c: Coincident(g2,g3)
    c: Coincident(g3,g0)
    c: Horizontal(g0)
    c: Horizontal(g2)
    c: Vertical(g1)
    c: Vertical(g3)
    c: DistanceX(g0,g-3) = 3
    c: DistanceY(g-3,g0) = 4
    c: DistanceX(g-4,g1) = 4
    c: DistanceY(g1,g-4) = 3
FEATURE [PartDesign::Pad] Pad018
  Direction = (1,1,1)
  Length = 44
  Length2 = 100
  Profile = -> Sketch023
  Reversed = true
  Type = 0
FEATURE [Sketcher::SketchObject] Sketch024
  ExternalGeometry = -> [ShapeBinder002]
  FullyConstrained = true
  MapMode = 5
  Placement = pos=(0,0,-17) rot=(1,0,0;3.14159rad)
  Support = -> [Pad018]
  sketch-geometry (4):
    g0: LineSegment StartX=-45.7 StartY=50.2 StartZ=0 EndX=46.7 EndY=50.2 EndZ=0
    g1: LineSegment StartX=46.7 StartY=50.2 StartZ=0 EndX=46.7 EndY=-51.2 EndZ=0
    g2: LineSegment StartX=46.7 StartY=-51.2 StartZ=0 EndX=-45.7 EndY=-51.2 EndZ=0
    g3: LineSegment StartX=-45.7 StartY=-51.2 StartZ=0 EndX=-45.7 EndY=50.2 EndZ=0
  constraints (12):
    c: Coincident(g0,g1)
    c: Coincident(g1,g2)
    c: Coincident(g2,g3)
    c: Coincident(g3,g0)
    c: Horizontal(g0)
    c: Horizontal(g2)
    c: Vertical(g1)
    c: Vertical(g3)
    c: DistanceX(g-4,g1) = 1.2
    c: DistanceY(g1,g-4) = 1.2
    c: DistanceY(g-3,g0) = 0.2
    c: DistanceX(g0,g-3) = 0.2
FEATURE [PartDesign::Pocket] Pocket003
  BaseFeature = -> Pad018
  Length = 42
  Length2 = 100
  Profile = -> Sketch024
  Type = 0
FEATURE [Sketcher::SketchObject] Sketch025
  ExternalGeometry = -> [Pocket003]
  FullyConstrained = true
  MapMode = 5
  Placement = pos=(0,0,-17) rot=(1,0,0;3.14159rad)
  Support = -> [Pocket003]
  sketch-geometry (8):
    g0: LineSegment StartX=-48.5 StartY=26 StartZ=0 EndX=-45.7 EndY=26 EndZ=0
    g1: LineSegment StartX=-45.7 StartY=26 StartZ=0 EndX=-45.7 EndY=-26 EndZ=0
    g2: LineSegment StartX=-45.7 StartY=-26 StartZ=0 EndX=-48.5 EndY=-26 EndZ=0
    g3: LineSegment StartX=-48.5 StartY=-26 StartZ=0 EndX=-48.5 EndY=26 EndZ=0
    g4: LineSegment StartX=46.7 StartY=26 StartZ=0 EndX=49.5 EndY=26 EndZ=0
    g5: LineSegment StartX=49.5 StartY=26 StartZ=0 EndX=49.5 EndY=-26 EndZ=0
    g6: LineSegment StartX=49.5 StartY=-26 StartZ=0 EndX=46.7 EndY=-26 EndZ=0
    g7: LineSegment StartX=46.7 StartY=-26 StartZ=0 EndX=46.7 EndY=26 EndZ=0
  constraints (23):
    c: Coincident(g0,g1)
    c: Coincident(g1,g2)
    c: Coincident(g2,g3)
    c: Coincident(g3,g0)
    c: Horizontal(g0)
    c: Horizontal(g2)
    c: Vertical(g1)
    c: PointOnObject(g0,g-3)
    c: PointOnObject(g1,g-4)
    c: Coincident(g4,g5)
    c: Coincident(g5,g6)
    c: Coincident(g6,g7)
    c: Coincident(g7,g4)
    c: Horizontal(g4)
    c: Horizontal(g6)
    c: Vertical(g5)
    c: Vertical(g7)
    c: PointOnObject(g4,g-5)
    c: PointOnObject(g5,g-6)
    c: Symmetric(g0,g2,g-1)
    c: Horizontal(g0,g4)
    c: Equal(g1,g7)
    c: DistanceY(g-1,g0) = 26
FEATURE [PartDesign::Pocket] Pocket004
  BaseFeature = -> Pocket003
  Length = 6.2
  Length2 = 100
  Profile = -> Sketch025
  Type = 0
FEATURE [Sketcher::SketchObject] Sketch026
  ExternalGeometry = -> [Pocket004]
  FullyConstrained = true
  MapMode = 5
  Placement = pos=(0,0,27) rot=(0,0,1;0rad)
  Support = -> [Pocket004]
  sketch-geometry (4):
    g0: LineSegment StartX=-42.5 StartY=49 StartZ=0 EndX=44.5 EndY=49 EndZ=0
    g1: LineSegment StartX=44.5 StartY=49 StartZ=0 EndX=44.5 EndY=-5 EndZ=0
    g2: LineSegment StartX=44.5 StartY=-5 StartZ=0 EndX=-42.5 EndY=-5 EndZ=0
    g3: LineSegment StartX=-42.5 StartY=-5 StartZ=0 EndX=-42.5 EndY=49 EndZ=0
  constraints (12):
    c: Coincident(g0,g1)
    c: Coincident(g1,g2)
    c: Coincident(g2,g3)
    c: Coincident(g3,g0)
    c: Horizontal(g0)
    c: Horizontal(g2)
    c: Vertical(g1)
    c: Vertical(g3)
    c: DistanceY(g3,g3) = 54
    c: DistanceY(g0,g-3) = 5
    c: DistanceX(g-3,g0) = 6
    c: DistanceX(g0,g-4) = 5
FEATURE [PartDesign::Pocket] Pocket005
  BaseFeature = -> Pocket004
  Length = 2
  Length2 = 100
  Profile = -> Sketch026
  Type = 0
FEATURE [Sketcher::SketchObject] Sketch027
  ExternalGeometry = -> [Pocket005]
  FullyConstrained = true
  MapMode = 5
  Placement = pos=(-45.7,0,0) rot=(0.57735,0.57735,0.57735;2.0944rad)
  Support = -> [Pocket005]
  sketch-geometry (8):
    g0: LineSegment StartX=-50.2 StartY=-17 StartZ=0 EndX=-43.2 EndY=-17 EndZ=0
    g1: LineSegment StartX=-43.2 StartY=-17 StartZ=0 EndX=-43.2 EndY=-5 EndZ=0
    g2: LineSegment StartX=-43.2 StartY=-5 StartZ=0 EndX=-50.2 EndY=-5 EndZ=0
    g3: LineSegment StartX=-50.2 StartY=-5 StartZ=0 EndX=-50.2 EndY=-17 EndZ=0
    g4: LineSegment StartX=51.2 StartY=-17 StartZ=0 EndX=44.2 EndY=-17 EndZ=0
    g5: LineSegment StartX=44.2 StartY=-17 StartZ=0 EndX=44.2 EndY=-5 EndZ=0
    g6: LineSegment StartX=44.2 StartY=-5 StartZ=0 EndX=51.2 EndY=-5 EndZ=0
    g7: LineSegment StartX=51.2 StartY=-5 StartZ=0 EndX=51.2 EndY=-17 EndZ=0
  constraints (22):
    c: Coincident(g0,g1)
    c: Coincident(g1,g2)
    c: Coincident(g2,g3)
    c: Coincident(g3,g0)
    c: Horizontal(g0)
    c: Horizontal(g2)
    c: Vertical(g1)
    c: Vertical(g3)
    c: Coincident(g0,g-3)
    c: Coincident(g4,g5)
    c: Coincident(g5,g6)
    c: Coincident(g6,g7)
    c: Coincident(g7,g4)
    c: Horizontal(g4)
    c: Horizontal(g6)
    c: Vertical(g5)
    c: Vertical(g7)
    c: Coincident(g4,g-4)
    c: Equal(g2,g6)
    c: DistanceX(g2,g2) = 7
    c: Equal(g1,g5)
    c: DistanceY(g3,g3) = 12
FEATURE [PartDesign::Pad] Pad019
  BaseFeature = -> Pocket005
  Direction = (1,1,1)
  Length = 2
  Length2 = 100
  Profile = -> Sketch027
  Type = 0
FEATURE [Sketcher::SketchObject] Sketch028
  ExternalGeometry = -> [Pad019]
  FullyConstrained = true
  MapMode = 5
  Placement = pos=(46.7,0,0) rot=(0.57735,-0.57735,-0.57735;2.0944rad)
  Support = -> [Pad019]
  sketch-geometry (8):
    g0: LineSegment StartX=-51.2 StartY=-17 StartZ=0 EndX=-44.2 EndY=-17 EndZ=0
    g1: LineSegment StartX=-44.2 StartY=-17 StartZ=0 EndX=-44.2 EndY=-5 EndZ=0
    g2: LineSegment StartX=-44.2 StartY=-5 StartZ=0 EndX=-51.2 EndY=-5 EndZ=0
    g3: LineSegment StartX=-51.2 StartY=-5 StartZ=0 EndX=-51.2 EndY=-17 EndZ=0
    g4: LineSegment StartX=50.2 StartY=-17 StartZ=0 EndX=43.2 EndY=-17 EndZ=0
    g5: LineSegment StartX=43.2 StartY=-17 StartZ=0 EndX=43.2 EndY=-5 EndZ=0
    g6: LineSegment StartX=43.2 StartY=-5 StartZ=0 EndX=50.2 EndY=-5 EndZ=0
    g7: LineSegment StartX=50.2 StartY=-5 StartZ=0 EndX=50.2 EndY=-17 EndZ=0
  constraints (22):
    c: Coincident(g0,g1)
    c: Coincident(g1,g2)
    c: Coincident(g2,g3)
    c: Coincident(g3,g0)
    c: Horizontal(g0)
    c: Horizontal(g2)
    c: Vertical(g1)
    c: Vertical(g3)
    c: Coincident(g0,g-3)
    c: Coincident(g4,g5)
    c: Coincident(g5,g6)
    c: Coincident(g6,g7)
    c: Coincident(g7,g4)
    c: Horizontal(g4)
    c: Horizontal(g6)
    c: Vertical(g5)
    c: Vertical(g7)
    c: Coincident(g4,g-4)
    c: Equal(g2,g6)
    c: Equal(g1,g5)
    c: DistanceX(g2,g2) = 7
    c: DistanceY(g3,g3) = 12
FEATURE [PartDesign::Pad] Pad020
  BaseFeature = -> Pad019
  Direction = (1,1,1)
  Length = 2
  Length2 = 100
  Profile = -> Sketch028
  Type = 0
FEATURE [Sketcher::SketchObject] Sketch029
  ExternalGeometry = -> [ShapeBinder004]
  FullyConstrained = true
  MapMode = 5
  Placement = pos=(49.5,0,0) rot=(0.57735,0.57735,0.57735;2.0944rad)
  Support = -> [Pad020]
  sketch-geometry (2):
    g0: Circle CenterX=-47 CenterY=-12 CenterZ=0 NormalX=0 NormalY=0 NormalZ=1 AngleXU=0 Radius=1.6
    g1: Circle CenterX=48 CenterY=-12 CenterZ=0 NormalX=0 NormalY=0 NormalZ=1 AngleXU=0 Radius=1.6
  constraints (4):
    c: Equal(g1,g0)
    c: Radius(g0) = 1.6
    c: Symmetric(g-4,g-3,g0)
    c: Symmetric(g-5,g-6,g1)
FEATURE [PartDesign::Pocket] Pocket006
  BaseFeature = -> Pad020
  Length = 5
  Length2 = 100
  Profile = -> Sketch029
  Type = 1
FEATURE [Sketcher::SketchObject] Sketch030
  ExternalGeometry = -> [Pocket006]
  FullyConstrained = true
  MapMode = 5
  Placement = pos=(49.5,0,0) rot=(0.57735,0.57735,0.57735;2.0944rad)
  Support = -> [Pocket006]
  sketch-geometry (2):
    g0: Circle CenterX=48 CenterY=-12 CenterZ=0 NormalX=0 NormalY=0 NormalZ=1 AngleXU=0 Radius=3.2
    g1: Circle CenterX=-47 CenterY=-12 CenterZ=0 NormalX=0 NormalY=0 NormalZ=1 AngleXU=0 Radius=3.2
  constraints (4):
    c: Coincident(g0,g-3)
    c: Coincident(g1,g-4)
    c: Equal(g0,g1)
    c: Radius(g0) = 3.2
FEATURE [PartDesign::Pocket] Pocket007
  BaseFeature = -> Pocket006
  Length = 2.2
  Length2 = 100
  Profile = -> Sketch030
  Type = 0
FEATURE [Sketcher::SketchObject] Sketch031
  ExternalGeometry = -> [Pocket007]
  FullyConstrained = true
  MapMode = 5
  Placement = pos=(-48.5,0,0) rot=(0.57735,-0.57735,-0.57735;2.0944rad)
  Support = -> [Pocket007]
  sketch-geometry (2):
    g0: Circle CenterX=47 CenterY=-12 CenterZ=0 NormalX=0 NormalY=0 NormalZ=1 AngleXU=0 Radius=3.2
    g1: Circle CenterX=-48 CenterY=-12 CenterZ=0 NormalX=0 NormalY=0 NormalZ=1 AngleXU=0 Radius=3.2
  constraints (4):
    c: Coincident(g0,g-3)
    c: Coincident(g1,g-4)
    c: Equal(g0,g1)
    c: Radius(g0) = 3.2
FEATURE [PartDesign::Pocket] Pocket008
  BaseFeature = -> Pocket007
  Length = 2.2
  Length2 = 100
  Profile = -> Sketch031
  Type = 0
FEATURE [Sketcher::SketchObject] Sketch032
  ExternalGeometry = -> [Pocket008]
  FullyConstrained = true
  MapMode = 5
  Placement = pos=(-48.5,0,0) rot=(0.57735,-0.57735,-0.57735;2.0944rad)
  Support = -> [Pocket008]
  sketch-geometry (16):
    g0: LineSegment StartX=-44.2 StartY=18.2 StartZ=0 EndX=-34.8 EndY=18.2 EndZ=0
    g1: LineSegment StartX=-34.8 StartY=18.2 StartZ=0 EndX=-34.8 EndY=14.4 EndZ=0
    g2: LineSegment StartX=-34.8 StartY=14.4 StartZ=0 EndX=-44.2 EndY=14.4 EndZ=0
    g3: LineSegment StartX=-44.2 StartY=14.4 StartZ=0 EndX=-44.2 EndY=18.2 EndZ=0
    g4: LineSegment StartX=-42.2 StartY=5.2 StartZ=0 EndX=-32.8 EndY=5.2 EndZ=0
    g5: LineSegment StartX=-32.8 StartY=5.2 StartZ=0 EndX=-32.8 EndY=1.4 EndZ=0
    g6: LineSegment StartX=-32.8 StartY=1.4 StartZ=0 EndX=-42.2 EndY=1.4 EndZ=0
    g7: LineSegment StartX=-42.2 StartY=1.4 StartZ=0 EndX=-42.2 EndY=5.2 EndZ=0
    g8: LineSegment StartX=-29.2 StartY=4.4 StartZ=0 EndX=-21.4 EndY=4.4 EndZ=0
    g9: LineSegment StartX=-21.4 StartY=4.4 StartZ=0 EndX=-21.4 EndY=1.4 EndZ=0
    g10: LineSegment StartX=-21.4 StartY=1.4 StartZ=0 EndX=-29.2 EndY=1.4 EndZ=0
    g11: LineSegment StartX=-29.2 StartY=1.4 StartZ=0 EndX=-29.2 EndY=4.4 EndZ=0
    g12: LineSegment StartX=26.6 StartY=17.6 StartZ=0 EndX=33.6 EndY=17.6 EndZ=0
    g13: LineSegment StartX=33.6 StartY=17.6 StartZ=0 EndX=33.6 EndY=10.6 EndZ=0
    g14: LineSegment StartX=33.6 StartY=10.6 StartZ=0 EndX=26.6 EndY=10.6 EndZ=0
    g15: LineSegment StartX=26.6 StartY=10.6 StartZ=0 EndX=26.6 EndY=17.6 EndZ=0
  constraints (48):
    c: Coincident(g0,g1)
    c: Coincident(g1,g2)
    c: Coincident(g2,g3)
    c: Coincident(g3,g0)
    c: Horizontal(g0)
    c: Horizontal(g2)
    c: Vertical(g1)
    c: Vertical(g3)
    c: Coincident(g4,g5)
    c: Coincident(g5,g6)
    c: Coincident(g6,g7)
    c: Coincident(g7,g4)
    c: Horizontal(g4)
    c: Horizontal(g6)
    c: Vertical(g7)
    c: Coincident(g8,g9)
    c: Coincident(g9,g10)
    c: Coincident(g10,g11)
    c: Coincident(g11,g8)
    c: Horizontal(g8)
    c: Horizontal(g10)
    c: Vertical(g9)
    c: Vertical(g11)
    c: Coincident(g12,g13)
    c: Coincident(g13,g14)
    c: Coincident(g14,g15)
    c: Coincident(g15,g12)
    c: Vertical(g13)
    c: Vertical(g15)
    c: DistanceX(g6,g6) = 9.4
    c: DistanceX(g-3,g10) = 24.8
    c: DistanceX(g10,g10) = 7.8
    c: DistanceY(g9,g9) = 3
    c: DistanceX(g-3,g6) = 11.8
    c: Vertical(g5)
    c: DistanceY(g7,g7) = 3.8
    c: DistanceY(g-1,g6) = 1.4
    c: DistanceY(g-1,g10) = 1.4
    c: Equal(g3,g7)
    c: Equal(g4,g2)
    c: DistanceY(g0,g-3) = 8.8
    c: DistanceX(g-3,g0) = 9.8
    c: DistanceX(g12,g12) = 7
    c: DistanceY(g13,g13) = 7
    c: Horizontal(g12)
    c: Horizontal(g14)
    c: DistanceY(g-1,g13) = 10.6
    c: DistanceX(g13,g-4) = 19.4
FEATURE [PartDesign::Pocket] Pocket009
  BaseFeature = -> Pocket008
  Length = 2.8
  Length2 = 100
  Profile = -> Sketch032
  Type = 0
FEATURE [Sketcher::SketchObject] Sketch033
  ExternalGeometry = -> [Pocket009]
  FullyConstrained = true
  MapMode = 5
  Placement = pos=(0,-53,0) rot=(1,0,0;1.5708rad)
  Support = -> [Pocket009]
  sketch-geometry (4):
    g0: LineSegment StartX=-7.1 StartY=-1 StartZ=0 EndX=6.3 EndY=-1 EndZ=0
    g1: LineSegment StartX=6.3 StartY=-1 StartZ=0 EndX=6.3 EndY=-7 EndZ=0
    g2: LineSegment StartX=6.3 StartY=-7 StartZ=0 EndX=-7.1 EndY=-7 EndZ=0
    g3: LineSegment StartX=-7.1 StartY=-7 StartZ=0 EndX=-7.1 EndY=-1 EndZ=0
  constraints (12):
    c: Coincident(g0,g1)
    c: Coincident(g1,g2)
    c: Coincident(g2,g3)
    c: Coincident(g3,g0)
    c: Horizontal(g0)
    c: Horizontal(g2)
    c: Vertical(g1)
    c: Vertical(g3)
    c: DistanceX(g0,g0) = 13.4
    c: DistanceX(g-3,g2) = 41.4
    c: DistanceY(g1,g1) = 6
    c: DistanceY(g1,g-1) = 7
FEATURE [PartDesign::Pocket] Pocket010
  BaseFeature = -> Pocket009
  Length = 2.8
  Length2 = 100
  Profile = -> Sketch033
  Type = 0
FEATURE [Sketcher::SketchObject] Sketch034
  FullyConstrained = true
  MapMode = 5
  Support = -> [XY_Plane]
  sketch-geometry (28):
    g0: LineSegment StartX=-3 StartY=-15.5 StartZ=0 EndX=3 EndY=-15.5 EndZ=0
    g1: LineSegment StartX=3 StartY=-15.5 StartZ=0 EndX=3 EndY=-19 EndZ=0
    g2: LineSegment StartX=3 StartY=-19 StartZ=0 EndX=-3 EndY=-19 EndZ=0
    g3: LineSegment StartX=-3 StartY=-19 StartZ=0 EndX=-3 EndY=-15.5 EndZ=0
    g4: LineSegment StartX=-3 StartY=-38.5 StartZ=0 EndX=3 EndY=-38.5 EndZ=0
    g5: LineSegment StartX=3 StartY=-38.5 StartZ=0 EndX=3 EndY=-42 EndZ=0
    g6: LineSegment StartX=3 StartY=-42 StartZ=0 EndX=-3 EndY=-42 EndZ=0
    g7: LineSegment StartX=-3 StartY=-42 StartZ=0 EndX=-3 EndY=-38.5 EndZ=0
    g8: LineSegment StartX=-18 StartY=-27 StartZ=0 EndX=-12 EndY=-27 EndZ=0
    g9: LineSegment StartX=-12 StartY=-27 StartZ=0 EndX=-12 EndY=-30.5 EndZ=0
    g10: LineSegment StartX=-12 StartY=-30.5 StartZ=0 EndX=-18 EndY=-30.5 EndZ=0
    g11: LineSegment StartX=-18 StartY=-30.5 StartZ=0 EndX=-18 EndY=-27 EndZ=0
    g12: LineSegment StartX=12 StartY=-27 StartZ=0 EndX=18 EndY=-27 EndZ=0
    g13: LineSegment StartX=18 StartY=-27 StartZ=0 EndX=18 EndY=-30.5 EndZ=0
    g14: LineSegment StartX=18 StartY=-30.5 StartZ=0 EndX=12 EndY=-30.5 EndZ=0
    g15: LineSegment StartX=12 StartY=-30.5 StartZ=0 EndX=12 EndY=-27 EndZ=0
    g16: LineSegment StartX=-40.5 StartY=-26.6 StartZ=0 EndX=-33.5 EndY=-26.6 EndZ=0
    g17: LineSegment StartX=-33.5 StartY=-26.6 StartZ=0 EndX=-33.5 EndY=-33.6 EndZ=0
    g18: LineSegment StartX=-33.5 StartY=-33.6 StartZ=0 EndX=-40.5 EndY=-33.6 EndZ=0
    g19: LineSegment StartX=-40.5 StartY=-33.6 StartZ=0 EndX=-40.5 EndY=-26.6 EndZ=0
    g20: LineSegment StartX=-45.5 StartY=-8 StartZ=0 EndX=45.5 EndY=-8 EndZ=0
    g21: LineSegment StartX=45.5 StartY=-8 StartZ=0 EndX=45.5 EndY=-50 EndZ=0
    g22: LineSegment StartX=45.5 StartY=-50 StartZ=0 EndX=-45.5 EndY=-50 EndZ=0
    g23: LineSegment StartX=-45.5 StartY=-50 StartZ=0 EndX=-45.5 EndY=-8 EndZ=0
    g24: LineSegment StartX=27.5 StartY=-16 StartZ=0 EndX=45.5 EndY=-16 EndZ=0
    g25: LineSegment StartX=45.5 StartY=-16 StartZ=0 EndX=45.5 EndY=-41 EndZ=0
    g26: LineSegment StartX=45.5 StartY=-41 StartZ=0 EndX=27.5 EndY=-41 EndZ=0
    g27: LineSegment StartX=27.5 StartY=-41 StartZ=0 EndX=27.5 EndY=-16 EndZ=0
  constraints (81):
    c: Coincident(g0,g1)
    c: Coincident(g1,g2)
    c: Coincident(g2,g3)
    c: Coincident(g3,g0)
    c: Horizontal(g2)
    c: Vertical(g1)
    c: Vertical(g3)
    c: Coincident(g4,g5)
    c: Coincident(g5,g6)
    c: Coincident(g6,g7)
    c: Coincident(g7,g4)
    c: Horizontal(g4)
    c: Horizontal(g6)
    c: Vertical(g5)
    c: Vertical(g7)
    c: Coincident(g8,g9)
    c: Coincident(g9,g10)
    c: Coincident(g10,g11)
    c: Coincident(g11,g8)
    c: Horizontal(g8)
    c: Horizontal(g10)
    c: Vertical(g9)
    c: Vertical(g11)
    c: Coincident(g12,g13)
    c: Coincident(g13,g14)
    c: Coincident(g14,g15)
    c: Coincident(g15,g12)
    c: Horizontal(g12)
    c: Horizontal(g14)
    c: Vertical(g13)
    c: Vertical(g15)
    c: Coincident(g16,g17)
    c: Coincident(g17,g18)
    c: Coincident(g18,g19)
    c: Coincident(g19,g16)
    c: Horizontal(g16)
    c: Horizontal(g18)
    c: Vertical(g17)
    c: Vertical(g19)
    c: Equal(g11,g3)
    c: Equal(g3,g15)
    c: Equal(g15,g7)
    c: Equal(g8,g0)
    c: Equal(g0,g12)
    c: Equal(g12,g4)
    c: Vertical(g4,g2)
    c: DistanceY(g13,g13) = 3.5
    c: DistanceX(g14,g14) = 6
    c: DistanceY(g19,g19) = 7
    c: DistanceX(g16,g16) = 7
    c: Coincident(g20,g21)
    c: Coincident(g21,g22)
    c: Coincident(g22,g23)
    c: Coincident(g23,g20)
    c: Horizontal(g22)
    c: Vertical(g21)
    c: Vertical(g23)
    c: Symmetric(g20,g20,g-2)
    c: DistanceX(g20,g20) = 91
    c: DistanceY(g20,g-1) = 8
    c: DistanceY(g21,g21) = 42
    c: Symmetric(g0,g0,g-2)
    c: DistanceY(g12,g20) = 19
    c: Symmetric(g9,g14,g-2)
    c: Coincident(g24,g25)
    c: Coincident(g25,g26)
    c: Coincident(g26,g27)
    c: Coincident(g27,g24)
    c: Horizontal(g24)
    c: Horizontal(g26)
    c: Vertical(g25)
    c: Vertical(g27)
    c: DistanceX(g24,g24) = 18
    c: DistanceY(g25,g25) = 25
    c: PointOnObject(g25,g21)
    c: DistanceX(g-1,g14) = 12
    c: DistanceY(g8,g2) = 8
    c: DistanceY(g4,g10) = 8
    c: DistanceY(g24,g20) = 8
    c: DistanceY(g22,g18) = 16.4
    c: DistanceX(g22,g18) = 5
FEATURE [PartDesign::Body] Body  label="Guide"
  Group = -> [Sketch,Sketch016,Sketch034]
  Origin = -> Origin
FEATURE [PartDesign::ShapeBinder] ShapeBinder005
  Support = -> [Sketch034]
  TraceSupport = false
FEATURE [Sketcher::SketchObject] Sketch035
  ExternalGeometry = -> [ShapeBinder005]
  FullyConstrained = true
  MapMode = 5
  Placement = pos=(0,0,10.2) rot=(0,0,1;0rad)
  Support = -> [Pad014]
  sketch-geometry (16):
    g0: LineSegment StartX=-18 StartY=-27 StartZ=0 EndX=-12 EndY=-27 EndZ=0
    g1: LineSegment StartX=-12 StartY=-27 StartZ=0 EndX=-12 EndY=-30.5 EndZ=0
    g2: LineSegment StartX=-12 StartY=-30.5 StartZ=0 EndX=-18 EndY=-30.5 EndZ=0
    g3: LineSegment StartX=-18 StartY=-30.5 StartZ=0 EndX=-18 EndY=-27 EndZ=0
    g4: LineSegment StartX=-3 StartY=-15.5 StartZ=0 EndX=3 EndY=-15.5 EndZ=0
    g5: LineSegment StartX=3 StartY=-15.5 StartZ=0 EndX=3 EndY=-19 EndZ=0
    g6: LineSegment StartX=3 StartY=-19 StartZ=0 EndX=-3 EndY=-19 EndZ=0
    g7: LineSegment StartX=-3 StartY=-19 StartZ=0 EndX=-3 EndY=-15.5 EndZ=0
    g8: LineSegment StartX=12 StartY=-27 StartZ=0 EndX=18 EndY=-27 EndZ=0
    g9: LineSegment StartX=18 StartY=-27 StartZ=0 EndX=18 EndY=-30.5 EndZ=0
    g10: LineSegment StartX=18 StartY=-30.5 StartZ=0 EndX=12 EndY=-30.5 EndZ=0
    g11: LineSegment StartX=12 StartY=-30.5 StartZ=0 EndX=12 EndY=-27 EndZ=0
    g12: LineSegment StartX=-3 StartY=-38.5 StartZ=0 EndX=3 EndY=-38.5 EndZ=0
    g13: LineSegment StartX=3 StartY=-38.5 StartZ=0 EndX=3 EndY=-42 EndZ=0
    g14: LineSegment StartX=3 StartY=-42 StartZ=0 EndX=-3 EndY=-42 EndZ=0
    g15: LineSegment StartX=-3 StartY=-42 StartZ=0 EndX=-3 EndY=-38.5 EndZ=0
  constraints (40):
    c: Coincident(g0,g1)
    c: Coincident(g1,g2)
    c: Coincident(g2,g3)
    c: Coincident(g3,g0)
    c: Horizontal(g0)
    c: Horizontal(g2)
    c: Vertical(g1)
    c: Vertical(g3)
    c: Coincident(g0,g-3)
    c: Coincident(g1,g-4)
    c: Coincident(g4,g5)
    c: Coincident(g5,g6)
    c: Coincident(g6,g7)
    c: Coincident(g7,g4)
    c: Horizontal(g4)
    c: Horizontal(g6)
    c: Vertical(g5)
    c: Vertical(g7)
    c: Coincident(g4,g-5)
    c: Coincident(g5,g-6)
    c: Coincident(g8,g9)
    c: Coincident(g9,g10)
    c: Coincident(g10,g11)
    c: Coincident(g11,g8)
    c: Horizontal(g8)
    c: Horizontal(g10)
    c: Vertical(g9)
    c: Vertical(g11)
    c: Coincident(g8,g-7)
    c: Coincident(g9,g-8)
    c: Coincident(g12,g13)
    c: Coincident(g13,g14)
    c: Coincident(g14,g15)
    c: Coincident(g15,g12)
    c: Horizontal(g12)
    c: Horizontal(g14)
    c: Vertical(g13)
    c: Vertical(g15)
    c: Coincident(g12,g-9)
    c: Coincident(g13,g-10)
FEATURE [PartDesign::Pad] Pad021
  BaseFeature = -> Pad014
  Direction = (1,1,1)
  Length = 4.2
  Length2 = 100
  Profile = -> Sketch035
  Type = 0
FEATURE [Sketcher::SketchObject] Sketch036
  ExternalGeometry = -> [ShapeBinder005]
  FullyConstrained = true
  MapMode = 5
  Placement = pos=(0,0,10.2) rot=(0,0,1;0rad)
  Support = -> [Pad021]
  sketch-geometry (4):
    g0: LineSegment StartX=-40.5 StartY=-26.6 StartZ=0 EndX=-33.5 EndY=-26.6 EndZ=0
    g1: LineSegment StartX=-33.5 StartY=-26.6 StartZ=0 EndX=-33.5 EndY=-33.6 EndZ=0
    g2: LineSegment StartX=-33.5 StartY=-33.6 StartZ=0 EndX=-40.5 EndY=-33.6 EndZ=0
    g3: LineSegment StartX=-40.5 StartY=-33.6 StartZ=0 EndX=-40.5 EndY=-26.6 EndZ=0
  constraints (10):
    c: Coincident(g0,g1)
    c: Coincident(g1,g2)
    c: Coincident(g2,g3)
    c: Coincident(g3,g0)
    c: Horizontal(g0)
    c: Horizontal(g2)
    c: Vertical(g1)
    c: Vertical(g3)
    c: Coincident(g0,g-3)
    c: Coincident(g1,g-4)
FEATURE [PartDesign::Pad] Pad022
  BaseFeature = -> Pad021
  Direction = (1,1,1)
  Length = 7.4
  Length2 = 100
  Profile = -> Sketch036
  Type = 0
FEATURE [Sketcher::SketchObject] Sketch037
  ExternalGeometry = -> [ShapeBinder005]
  FullyConstrained = true
  MapMode = 5
  Placement = pos=(0,0,10.2) rot=(0,0,1;0rad)
  Support = -> [Pad022]
  sketch-geometry (4):
    g0: LineSegment StartX=27.5 StartY=-16 StartZ=0 EndX=45.5 EndY=-16 EndZ=0
    g1: LineSegment StartX=45.5 StartY=-16 StartZ=0 EndX=45.5 EndY=-41 EndZ=0
    g2: LineSegment StartX=45.5 StartY=-41 StartZ=0 EndX=27.5 EndY=-41 EndZ=0
    g3: LineSegment StartX=27.5 StartY=-41 StartZ=0 EndX=27.5 EndY=-16 EndZ=0
  constraints (10):
    c: Coincident(g0,g1)
    c: Coincident(g1,g2)
    c: Coincident(g2,g3)
    c: Coincident(g3,g0)
    c: Horizontal(g0)
    c: Horizontal(g2)
    c: Vertical(g1)
    c: Vertical(g3)
    c: Coincident(g0,g-3)
    c: Coincident(g1,g-4)
FEATURE [PartDesign::Pad] Pad023
  BaseFeature = -> Pad022
  Direction = (1,1,1)
  Length = 1.6
  Length2 = 100
  Profile = -> Sketch037
  Type = 0
FEATURE [Sketcher::SketchObject] Sketch038
  ExternalGeometry = -> [Pad023]
  FullyConstrained = true
  MapMode = 5
  Placement = pos=(0,0,11.8) rot=(0,0,1;0rad)
  Support = -> [Pad023]
  sketch-geometry (4):
    g0: LineSegment StartX=29 StartY=-24 StartZ=0 EndX=44 EndY=-24 EndZ=0
    g1: LineSegment StartX=44 StartY=-24 StartZ=0 EndX=44 EndY=-39 EndZ=0
    g2: LineSegment StartX=44 StartY=-39 StartZ=0 EndX=29 EndY=-39 EndZ=0
    g3: LineSegment StartX=29 StartY=-39 StartZ=0 EndX=29 EndY=-24 EndZ=0
  constraints (12):
    c: Coincident(g0,g1)
    c: Coincident(g1,g2)
    c: Coincident(g2,g3)
    c: Coincident(g3,g0)
    c: Horizontal(g0)
    c: Horizontal(g2)
    c: Vertical(g1)
    c: Vertical(g3)
    c: DistanceX(g0,g0) = 15
    c: DistanceY(g3,g3) = 15
    c: DistanceY(g-3,g2) = 2
    c: DistanceX(g-3,g2) = 1.5
FEATURE [PartDesign::Pad] Pad024
  BaseFeature = -> Pad023
  Direction = (1,1,1)
  Length = 5.8
  Length2 = 100
  Profile = -> Sketch038
  Type = 0
FEATURE [PartDesign::Body] Body001  label="Body"
  Group = -> [ShapeBinder,Sketch001,Pad,Sketch002,Pad001,Sketch003,Pad002,Sketch004,Pad003,Sketch005,Pad004,Sketch006,Pad005,Sketch007,Pad006,Sketch008,Pad007,Sketch009,Pad008,Sketch010,Pad009,Sketch011,Pad010,Sketch012,Pad011,Sketch013,Pad012,Sketch014,Pad013,Sketch015,Pad014,ShapeBinder005,Sketch035,Pad021,Sketch036,Pad022,Sketch037,Pad023,Sketch038,Pad024]
  Origin = -> Origin001
  Tip = -> Pad024
FEATURE [PartDesign::ShapeBinder] ShapeBinder006
  Support = -> [Sketch034]
  TraceSupport = false
FEATURE [Sketcher::SketchObject] Sketch039
  AttachmentOffset = pos=(0,0,14.6) rot=(0,0,1;0rad)
  ExternalGeometry = -> [ShapeBinder006]
  FullyConstrained = true
  MapMode = 5
  Placement = pos=(0,0,14.6) rot=(0,0,1;0rad)
  Support = -> [XY_Plane004]
  sketch-geometry (20):
    g0: LineSegment StartX=-3 StartY=-11.5 StartZ=0 EndX=3 EndY=-11.5 EndZ=0
    g1: LineSegment StartX=7 StartY=-15.5 StartZ=0 EndX=7 EndY=-23 EndZ=0
    g2: LineSegment StartX=3 StartY=-46 StartZ=0 EndX=-3 EndY=-46 EndZ=0
    g3: LineSegment StartX=-7 StartY=-42 StartZ=0 EndX=-7 EndY=-34.5 EndZ=0
    g4: LineSegment StartX=-18 StartY=-23 StartZ=0 EndX=-7 EndY=-23 EndZ=0
    g5: LineSegment StartX=22 StartY=-27 StartZ=0 EndX=22 EndY=-30.5 EndZ=0
    g6: LineSegment StartX=18 StartY=-34.5 StartZ=0 EndX=7 EndY=-34.5 EndZ=0
    g7: LineSegment StartX=-22 StartY=-30.5 StartZ=0 EndX=-22 EndY=-27 EndZ=0
    g8: ArcOfCircle CenterX=-18 CenterY=-27 CenterZ=0 NormalX=0 NormalY=0 NormalZ=1 AngleXU=0 Radius=4 StartAngle=1.5708 EndAngle=3.14159
    g9: ArcOfCircle CenterX=-18 CenterY=-30.5 CenterZ=0 NormalX=0 NormalY=0 NormalZ=1 AngleXU=0 Radius=4 StartAngle=3.14159 EndAngle=4.71239
    g10: ArcOfCircle CenterX=-3 CenterY=-42 CenterZ=0 NormalX=0 NormalY=0 NormalZ=1 AngleXU=0 Radius=4 StartAngle=3.14159 EndAngle=4.71239
    g11: ArcOfCircle CenterX=3 CenterY=-42 CenterZ=0 NormalX=0 NormalY=0 NormalZ=1 AngleXU=0 Radius=4 StartAngle=4.71239 EndAngle=6.28319
    g12: ArcOfCircle CenterX=18 CenterY=-30.5 CenterZ=0 NormalX=0 NormalY=0 NormalZ=1 AngleXU=0 Radius=4 StartAngle=4.71239 EndAngle=6.28319
    g13: ArcOfCircle CenterX=18 CenterY=-27 CenterZ=0 NormalX=0 NormalY=0 NormalZ=1 AngleXU=0 Radius=4 StartAngle=0 EndAngle=1.5708
    g14: ArcOfCircle CenterX=3 CenterY=-15.5 CenterZ=0 NormalX=0 NormalY=0 NormalZ=1 AngleXU=0 Radius=4 StartAngle=0 EndAngle=1.5708
    g15: ArcOfCircle CenterX=-3 CenterY=-15.5 CenterZ=0 NormalX=0 NormalY=0 NormalZ=1 AngleXU=0 Radius=4 StartAngle=1.5708 EndAngle=3.14159
    g16: LineSegment StartX=7 StartY=-23 StartZ=0 EndX=18 EndY=-23 EndZ=0
    g17: LineSegment StartX=-7 StartY=-23 StartZ=0 EndX=-7 EndY=-15.5 EndZ=0
    g18: LineSegment StartX=7 StartY=-34.5 StartZ=0 EndX=7 EndY=-42 EndZ=0
    g19: LineSegment StartX=-7 StartY=-34.5 StartZ=0 EndX=-18 EndY=-34.5 EndZ=0
  constraints (46):
    c: Horizontal(g0)
    c: Horizontal(g2)
    c: Vertical(g1)
    c: Vertical(g3)
    c: Horizontal(g6)
    c: Vertical(g5)
    c: Vertical(g7)
    c: Tangent(g4,g8) = 1.5708
    c: Tangent(g7,g8) = 1.5708
    c: Coincident(g19,g9) = 1.5708
    c: Tangent(g7,g9) = 1.5708
    c: Tangent(g2,g10) = 1.5708
    c: Tangent(g3,g10) = 1.5708
    c: Coincident(g18,g11) = 1.5708
    c: Tangent(g2,g11) = 1.5708
    c: Tangent(g5,g12) = 1.5708
    c: Tangent(g6,g12) = 1.5708
    c: Coincident(g16,g13) = 1.5708
    c: Tangent(g5,g13) = 1.5708
    c: Tangent(g0,g14) = 1.5708
    c: Tangent(g1,g14) = 1.5708
    c: Tangent(g0,g15) = 1.5708
    c: Coincident(g17,g15) = 1.5708
    c: Tangent(g4,g16)
    c: Coincident(g17,g4)
    c: Tangent(g3,g17)
    c: Coincident(g1,g16)
    c: Tangent(g1,g18)
    c: Coincident(g6,g18)
    c: Coincident(g19,g3)
    c: Tangent(g6,g19)
    c: Vertical(g12,g13)
    c: Horizontal(g10,g11)
    c: Horizontal(g9,g12)
    c: Horizontal(g4)
    c: Coincident(g-10,g8)
    c: Coincident(g9,g-9)
    c: Coincident(g13,g-5)
    c: Coincident(g15,g-3)
    c: Coincident(g14,g-4)
    c: Coincident(g10,g-8)
    c: Radius(g8) = 4
    c: Radius(g14) = 4
    c: Horizontal(g15,g15)
    c: Horizontal(g11,g11)
    c: Radius(g13) = 4
FEATURE [PartDesign::Pad] Pad025
  Direction = (1,1,1)
  Length = 12.6
  Length2 = 100
  Profile = -> Sketch039
  Type = 0
FEATURE [PartDesign::ShapeBinder] ShapeBinder007
  Support = -> [Sketch034]
  TraceSupport = false
FEATURE [Sketcher::SketchObject] Sketch040
  ExternalGeometry = -> [ShapeBinder007]
  FullyConstrained = true
  MapMode = 5
  Placement = pos=(0,0,27) rot=(0,0,1;0rad)
  Support = -> [Pocket010]
  sketch-geometry (23):
    g0: LineSegment StartX=-18 StartY=-22.6 StartZ=0 EndX=-7.4 EndY=-22.6 EndZ=0
    g1: LineSegment StartX=22.4 StartY=-27 StartZ=0 EndX=22.4 EndY=-30.5 EndZ=0
    g2: LineSegment StartX=18 StartY=-34.9 StartZ=0 EndX=7.4 EndY=-34.9 EndZ=0
    g3: LineSegment StartX=-22.4 StartY=-30.5 StartZ=0 EndX=-22.4 EndY=-27 EndZ=0
    g4: LineSegment StartX=-3 StartY=-11.1 StartZ=0 EndX=3 EndY=-11.1 EndZ=0
    g5: LineSegment StartX=7.4 StartY=-15.5 StartZ=0 EndX=7.4 EndY=-22.6 EndZ=0
    g6: LineSegment StartX=3 StartY=-46.4 StartZ=0 EndX=-3 EndY=-46.4 EndZ=0
    g7: LineSegment StartX=-7.4 StartY=-42 StartZ=0 EndX=-7.4 EndY=-34.9 EndZ=0
    g8: ArcOfCircle CenterX=-3 CenterY=-15.5 CenterZ=0 NormalX=0 NormalY=0 NormalZ=1 AngleXU=0 Radius=4.4 StartAngle=1.5708 EndAngle=3.14159
    g9: ArcOfCircle CenterX=3 CenterY=-15.5 CenterZ=0 NormalX=0 NormalY=0 NormalZ=1 AngleXU=0 Radius=4.4 StartAngle=0 EndAngle=1.5708
    g10: ArcOfCircle CenterX=-18 CenterY=-27 CenterZ=0 NormalX=0 NormalY=0 NormalZ=1 AngleXU=0 Radius=4.4 StartAngle=1.5708 EndAngle=3.14159
    g11: ArcOfCircle CenterX=-18 CenterY=-30.5 CenterZ=0 NormalX=0 NormalY=0 NormalZ=1 AngleXU=0 Radius=4.4 StartAngle=3.14159 EndAngle=4.71239
    g12: ArcOfCircle CenterX=-3 CenterY=-42 CenterZ=0 NormalX=0 NormalY=0 NormalZ=1 AngleXU=0 Radius=4.4 StartAngle=3.14159 EndAngle=4.71239
    g13: ArcOfCircle CenterX=3 CenterY=-42 CenterZ=0 NormalX=0 NormalY=0 NormalZ=1 AngleXU=0 Radius=4.4 StartAngle=4.71239 EndAngle=6.28319
    g14: ArcOfCircle CenterX=18 CenterY=-30.5 CenterZ=0 NormalX=0 NormalY=0 NormalZ=1 AngleXU=0 Radius=4.4 StartAngle=4.71239 EndAngle=6.28319
    g15: ArcOfCircle CenterX=18 CenterY=-27 CenterZ=0 NormalX=0 NormalY=0 NormalZ=1 AngleXU=0 Radius=4.4 StartAngle=2e-16 EndAngle=1.5708
    g16: LineSegment StartX=7.4 StartY=-22.6 StartZ=0 EndX=18 EndY=-22.6 EndZ=0
    g17: LineSegment StartX=-7.4 StartY=-22.6 StartZ=0 EndX=-7.4 EndY=-15.5 EndZ=0
    g18: LineSegment StartX=7.4 StartY=-34.9 StartZ=0 EndX=7.4 EndY=-42 EndZ=0
    g19: LineSegment StartX=-7.4 StartY=-34.9 StartZ=0 EndX=-18 EndY=-34.9 EndZ=0
    g20: Circle CenterX=28 CenterY=-10 CenterZ=0 NormalX=0 NormalY=0 NormalZ=1 AngleXU=0 Radius=1.2
    g21: Circle CenterX=34 CenterY=-10 CenterZ=0 NormalX=0 NormalY=0 NormalZ=1 AngleXU=0 Radius=1.2
    g22: Circle CenterX=40 CenterY=-10 CenterZ=0 NormalX=0 NormalY=0 NormalZ=1 AngleXU=0 Radius=1.2
  constraints (55):
    c: Horizontal(g0)
    c: Horizontal(g2)
    c: Vertical(g1)
    c: Vertical(g3)
    c: Horizontal(g4)
    c: Horizontal(g6)
    c: Vertical(g5)
    c: Vertical(g7)
    c: Tangent(g4,g8) = 1.5708
    c: Coincident(g17,g8) = 1.5708
    c: Tangent(g4,g9) = 1.5708
    c: Tangent(g5,g9) = 1.5708
    c: Tangent(g0,g10) = 1.5708
    c: Tangent(g3,g10) = 1.5708
    c: Coincident(g19,g11) = 1.5708
    c: Tangent(g3,g11) = 1.5708
    c: Tangent(g6,g12) = 1.5708
    c: Tangent(g7,g12) = 1.5708
    c: Coincident(g18,g13) = 1.5708
    c: Tangent(g6,g13) = 1.5708
    c: Tangent(g1,g14) = 1.5708
    c: Tangent(g2,g14) = 1.5708
    c: Coincident(g16,g15) = 1.5708
    c: Tangent(g1,g15) = 1.5708
    c: Tangent(g0,g16)
    c: Coincident(g17,g0)
    c: Tangent(g7,g17)
    c: Coincident(g5,g16)
    c: Tangent(g5,g18)
    c: Coincident(g2,g18)
    c: Coincident(g19,g7)
    c: Tangent(g2,g19)
    c: Equal(g8,g10)
    c: Equal(g10,g11)
    c: Equal(g11,g12)
    c: Radius(g15) = 4.4
    c: Vertical(g15,g15)
    c: Vertical(g11,g11)
    c: Horizontal(g8,g8)
    c: Horizontal(g13,g13)
    c: Coincident(g10,g-10)
    c: Coincident(g-3,g8)
    c: Coincident(g15,g-5)
    c: Coincident(g9,g-4)
    c: Coincident(g14,g-6)
    c: Coincident(g13,g-7)
    c: Equal(g20,g21)
    c: Equal(g21,g22)
    c: Horizontal(g20,g21)
    c: Horizontal(g21,g22)
    c: Radius(g22) = 1.2
    c: DistanceX(g21,g22) = 6
    c: DistanceX(g20,g21) = 6
    c: DistanceX(g-1,g20) = 28
    c: DistanceY(g22,g-1) = 10
FEATURE [PartDesign::Pocket] Pocket011
  BaseFeature = -> Pocket010
  Length = 2
  Length2 = 100
  Profile = -> Sketch040
  Type = 0
FEATURE [Sketcher::SketchObject] Sketch041
  ExternalGeometry = -> [Pad025]
  FullyConstrained = true
  MapMode = 5
  Placement = pos=(0,0,14.6) rot=(1,0,0;3.14159rad)
  Support = -> [Pad025]
  sketch-geometry (12):
    g0: LineSegment StartX=-17 StartY=36.5 StartZ=0 EndX=-9 EndY=36.5 EndZ=0
    g1: LineSegment StartX=17 StartY=36.5 StartZ=0 EndX=17 EndY=21 EndZ=0
    g2: LineSegment StartX=17 StartY=21 StartZ=0 EndX=9 EndY=21 EndZ=0
    g3: LineSegment StartX=-17 StartY=21 StartZ=0 EndX=-17 EndY=36.5 EndZ=0
    g4: LineSegment StartX=-9 StartY=41.5 StartZ=0 EndX=9 EndY=41.5 EndZ=0
    g5: LineSegment StartX=9 StartY=41.5 StartZ=0 EndX=9 EndY=36.5 EndZ=0
    g6: LineSegment StartX=9 StartY=16 StartZ=0 EndX=-9 EndY=16 EndZ=0
    g7: LineSegment StartX=-9 StartY=16 StartZ=0 EndX=-9 EndY=21 EndZ=0
    g8: LineSegment StartX=9 StartY=36.5 StartZ=0 EndX=17 EndY=36.5 EndZ=0
    g9: LineSegment StartX=-9 StartY=36.5 StartZ=0 EndX=-9 EndY=41.5 EndZ=0
    g10: LineSegment StartX=9 StartY=21 StartZ=0 EndX=9 EndY=16 EndZ=0
    g11: LineSegment StartX=-9 StartY=21 StartZ=0 EndX=-17 EndY=21 EndZ=0
  constraints (32):
    c: Coincident(g8,g1)
    c: Coincident(g1,g2)
    c: Coincident(g11,g3)
    c: Coincident(g3,g0)
    c: Horizontal(g0)
    c: Horizontal(g2)
    c: Vertical(g1)
    c: Vertical(g3)
    c: Coincident(g4,g5)
    c: Coincident(g10,g6)
    c: Coincident(g6,g7)
    c: Coincident(g9,g4)
    c: Horizontal(g4)
    c: Horizontal(g6)
    c: Vertical(g5)
    c: Vertical(g7)
    c: Tangent(g0,g8)
    c: Coincident(g9,g0)
    c: Tangent(g7,g9)
    c: Coincident(g5,g8)
    c: Tangent(g5,g10)
    c: Coincident(g2,g10)
    c: Coincident(g11,g7)
    c: Tangent(g2,g11)
    c: Equal(g7,g9)
    c: Equal(g0,g8)
    c: DistanceX(g-4,g5) = 2
    c: DistanceY(g-4,g5) = 2
    c: DistanceX(g0,g-3) = 2
    c: DistanceY(g2,g-5) = 2
    c: DistanceY(g1,g4) = 5
    c: DistanceX(g6,g1) = 8
FEATURE [PartDesign::Pad] Pad026
  BaseFeature = -> Pad025
  Direction = (1,1,1)
  Length = 10.2
  Length2 = 100
  Profile = -> Sketch041
  Reversed = true
  Type = 0
FEATURE [Sketcher::SketchObject] Sketch042
  ExternalGeometry = -> [Pad026]
  FullyConstrained = true
  MapMode = 5
  Placement = pos=(0,0,27.2) rot=(0,0,1;0rad)
  Support = -> [Pad026]
  sketch-geometry (12):
    g0: LineSegment StartX=0 StartY=-16.75 StartZ=0 EndX=-2.5 EndY=-21.0801 EndZ=0
    g1: LineSegment StartX=-2.5 StartY=-21.0801 StartZ=0 EndX=2.5 EndY=-21.0801 EndZ=0
    g2: LineSegment StartX=0 StartY=-16.75 StartZ=0 EndX=2.5 EndY=-21.0801 EndZ=0
    g3: LineSegment StartX=-2.5 StartY=-36.4199 StartZ=0 EndX=2.5 EndY=-36.4199 EndZ=0
    g4: LineSegment StartX=2.5 StartY=-36.4199 StartZ=0 EndX=0 EndY=-40.75 EndZ=0
    g5: LineSegment StartX=0 StartY=-40.75 StartZ=0 EndX=-2.5 EndY=-36.4199 EndZ=0
    g6: LineSegment StartX=-16.3301 StartY=-28.75 StartZ=0 EndX=-12 EndY=-26.25 EndZ=0
    g7: LineSegment StartX=-12 StartY=-26.25 StartZ=0 EndX=-12 EndY=-31.25 EndZ=0
    g8: LineSegment StartX=-12 StartY=-31.25 StartZ=0 EndX=-16.3301 EndY=-28.75 EndZ=0
    g9: LineSegment StartX=12 StartY=-26.25 StartZ=0 EndX=12 EndY=-31.25 EndZ=0
    g10: LineSegment StartX=12 StartY=-26.25 StartZ=0 EndX=16.3301 EndY=-28.75 EndZ=0
    g11: LineSegment StartX=12 StartY=-31.25 StartZ=0 EndX=16.3301 EndY=-28.75 EndZ=0
  constraints (36):
    c: Coincident(g1,g0)
    c: Horizontal(g1)
    c: Coincident(g2,g0)
    c: Coincident(g2,g1)
    c: Horizontal(g3)
    c: Coincident(g4,g3)
    c: Coincident(g5,g4)
    c: Coincident(g5,g3)
    c: Coincident(g7,g6)
    c: Vertical(g7)
    c: Coincident(g8,g7)
    c: Coincident(g8,g6)
    c: Vertical(g9)
    c: Coincident(g10,g9)
    c: Coincident(g11,g9)
    c: Coincident(g11,g10)
    c: Equal(g8,g6)
    c: Equal(g6,g7)
    c: Equal(g0,g1)
    c: Equal(g1,g2)
    c: Equal(g11,g10)
    c: Equal(g10,g9)
    c: Equal(g5,g3)
    c: Equal(g3,g4)
    c: Equal(g7,g1)
    c: Equal(g1,g9)
    c: Equal(g9,g3)
    c: PointOnObject(g4,g-2)
    c: PointOnObject(g0,g-2)
    c: Horizontal(g6,g10)
    c: DistanceY(g10,g0) = 12
    c: DistanceY(g4,g10) = 12
    c: DistanceX(g7,g4) = 12
    c: DistanceX(g4,g9) = 12
    c: DistanceY(g7,g7) = 5
    c: DistanceY(g6,g-3) = 5.75
FEATURE [PartDesign::Pocket] Pocket012
  BaseFeature = -> Pad026
  Length = 1
  Length2 = 100
  Profile = -> Sketch042
  Type = 0
FEATURE [Sketcher::SketchObject] Sketch043
  FullyConstrained = true
  MapMode = 5
  Placement = pos=(49.5,0,0) rot=(0.57735,0.57735,0.57735;2.0944rad)
  Support = -> [Pocket011]
  sketch-geometry (4):
    g0: LineSegment StartX=-42.6 StartY=1 StartZ=0 EndX=-34.6 EndY=1 EndZ=0
    g1: LineSegment StartX=-34.6 StartY=1 StartZ=0 EndX=-34.6 EndY=-5 EndZ=0
    g2: LineSegment StartX=-34.6 StartY=-5 StartZ=0 EndX=-42.6 EndY=-5 EndZ=0
    g3: LineSegment StartX=-42.6 StartY=-5 StartZ=0 EndX=-42.6 EndY=1 EndZ=0
  constraints (12):
    c: Coincident(g0,g1)
    c: Coincident(g1,g2)
    c: Coincident(g2,g3)
    c: Coincident(g3,g0)
    c: Horizontal(g0)
    c: Horizontal(g2)
    c: Vertical(g1)
    c: Vertical(g3)
    c: DistanceX(g0,g0) = 8
    c: DistanceY(g1,g1) = 6
    c: DistanceY(g-1,g0) = 1
    c: DistanceX(g0,g-1) = 34.6
FEATURE [PartDesign::Pocket] Pocket013
  BaseFeature = -> Pocket011
  Length = 5
  Length2 = 100
  Profile = -> Sketch043
  Type = 0
FEATURE [Sketcher::SketchObject] Sketch044
  ExternalGeometry = -> [Pocket013]
  FullyConstrained = true
  MapMode = 5
  Placement = pos=(46.7,0,0) rot=(0.57735,-0.57735,-0.57735;2.0944rad)
  Support = -> [Pocket013]
  sketch-geometry (4):
    g0: LineSegment StartX=28.6 StartY=1 StartZ=0 EndX=48.6 EndY=1 EndZ=0
    g1: LineSegment StartX=48.6 StartY=1 StartZ=0 EndX=48.6 EndY=-5 EndZ=0
    g2: LineSegment StartX=48.6 StartY=-5 StartZ=0 EndX=28.6 EndY=-5 EndZ=0
    g3: LineSegment StartX=28.6 StartY=-5 StartZ=0 EndX=28.6 EndY=1 EndZ=0
  constraints (12):
    c: Coincident(g0,g1)
    c: Coincident(g1,g2)
    c: Coincident(g2,g3)
    c: Coincident(g3,g0)
    c: Horizontal(g0)
    c: Horizontal(g2)
    c: Vertical(g1)
    c: Vertical(g3)
    c: PointOnObject(g-3,g0)
    c: PointOnObject(g-3,g2)
    c: DistanceX(g0,g-3) = 6
    c: DistanceX(g-4,g0) = 6
FEATURE [PartDesign::Pocket] Pocket014
  BaseFeature = -> Pocket013
  Length = 0.6
  Length2 = 100
  Profile = -> Sketch044
  Type = 0
FEATURE [Sketcher::SketchObject] Sketch045
  ExternalGeometry = -> [Pocket014]
  FullyConstrained = true
  MapMode = 5
  Placement = pos=(-45.7,0,0) rot=(0.57735,0.57735,0.57735;2.0944rad)
  Support = -> [Pocket014]
  sketch-geometry (4):
    g0: LineSegment StartX=-40.6 StartY=17.6 StartZ=0 EndX=-19.6 EndY=17.6 EndZ=0
    g1: LineSegment StartX=-19.6 StartY=17.6 StartZ=0 EndX=-19.6 EndY=10.6 EndZ=0
    g2: LineSegment StartX=-19.6 StartY=10.6 StartZ=0 EndX=-40.6 EndY=10.6 EndZ=0
    g3: LineSegment StartX=-40.6 StartY=10.6 StartZ=0 EndX=-40.6 EndY=17.6 EndZ=0
  constraints (12):
    c: Coincident(g0,g1)
    c: Coincident(g1,g2)
    c: Coincident(g2,g3)
    c: Coincident(g3,g0)
    c: Horizontal(g0)
    c: Horizontal(g2)
    c: Vertical(g1)
    c: Vertical(g3)
    c: PointOnObject(g-3,g0)
    c: PointOnObject(g-3,g2)
    c: DistanceX(g0,g-4) = 7
    c: DistanceX(g-3,g0) = 7
FEATURE [PartDesign::Pocket] Pocket015
  BaseFeature = -> Pocket014
  Length = 0.6
  Length2 = 100
  Profile = -> Sketch045
  Type = 0
FEATURE [PartDesign::Chamfer] Chamfer
  Angle = 45
  Base = -> Pocket015 [Edge68,Edge67,Edge69,Edge70]
  BaseFeature = -> Pocket015
  ChamferType = 0
  FlipDirection = false
  Size = 1
  Size2 = 1
  SupportTransform = false
FEATURE [Sketcher::SketchObject] Sketch047
  ExternalGeometry = -> [Chamfer]
  FullyConstrained = true
  MapMode = 5
  Placement = pos=(0,-50.2,0) rot=(0,0.707107,0.707107;3.14159rad)
  Support = -> [Chamfer]
  sketch-geometry (4):
    g0: LineSegment StartX=-7.3 StartY=-1e-15 StartZ=0 EndX=8.1 EndY=-1e-15 EndZ=0
    g1: LineSegment StartX=8.1 StartY=-1e-15 StartZ=0 EndX=8.1 EndY=-17 EndZ=0
    g2: LineSegment StartX=8.1 StartY=-17 StartZ=0 EndX=-7.3 EndY=-17 EndZ=0
    g3: LineSegment StartX=-7.3 StartY=-17 StartZ=0 EndX=-7.3 EndY=0 EndZ=0
  constraints (12):
    c: Coincident(g0,g1)
    c: Coincident(g1,g2)
    c: Coincident(g2,g3)
    c: Coincident(g3,g0)
    c: Horizontal(g0)
    c: Horizontal(g2)
    c: Vertical(g1)
    c: Vertical(g3)
    c: PointOnObject(g1,g-3)
    c: DistanceX(g2,g-5) = 1
    c: DistanceX(g-4,g1) = 1
    c: DistanceY(g-4,g0) = 1
FEATURE [PartDesign::Pocket] Pocket016
  BaseFeature = -> Chamfer
  Length = 0.6
  Length2 = 100
  Profile = -> Sketch047
  Type = 0
FEATURE [PartDesign::Chamfer] Chamfer001
  Angle = 45
  Base = -> Pocket016 [Edge312,Edge308,Edge319,Edge323]
  BaseFeature = -> Pocket016
  ChamferType = 0
  FlipDirection = false
  Size = 1.9
  Size2 = 1
  SupportTransform = false
FEATURE [Sketcher::SketchObject] Sketch048
  FullyConstrained = true
  MapMode = 5
  Placement = pos=(0,0,0) rot=(0.57735,0.57735,0.57735;2.0944rad)
  Support = -> [YZ_Plane005]
  sketch-geometry (4):
    g0: LineSegment StartX=-8 StartY=8 StartZ=0 EndX=8 EndY=8 EndZ=0
    g1: LineSegment StartX=8 StartY=8 StartZ=0 EndX=8 EndY=0 EndZ=0
    g2: LineSegment StartX=8 StartY=0 StartZ=0 EndX=-8 EndY=0 EndZ=0
    g3: LineSegment StartX=-8 StartY=0 StartZ=0 EndX=-8 EndY=8 EndZ=0
  constraints (11):
    c: Coincident(g0,g1)
    c: Coincident(g1,g2)
    c: Coincident(g2,g3)
    c: Coincident(g3,g0)
    c: Horizontal(g2)
    c: Vertical(g1)
    c: Vertical(g3)
    c: DistanceX(g0,g0) = 16
    c: DistanceY(g3,g3) = 8
    c: PointOnObject(g1,g-1)
    c: Symmetric(g0,g0,g-2)
FEATURE [PartDesign::Pad] Pad027
  Direction = (1,1,1)
  Length = 12
  Length2 = 0
  Placement = pos=(0,0,0) rot=(0.57735,0.57735,0.57735;2.0944rad)
  Profile = -> Sketch048
  Type = 0
FEATURE [Sketcher::SketchObject] Sketch049
  ExternalGeometry = -> [Pad027]
  FullyConstrained = true
  MapMode = 5
  Placement = pos=(12,-2.6e-15,2.6e-15) rot=(0.57735,0.57735,0.57735;2.0944rad)
  Support = -> [Pad027]
  sketch-geometry (4):
    g0: LineSegment StartX=-3.8 StartY=8 StartZ=0 EndX=3.8 EndY=8 EndZ=0
    g1: LineSegment StartX=3.8 StartY=8 StartZ=0 EndX=3.8 EndY=0 EndZ=0
    g2: LineSegment StartX=3.8 StartY=0 StartZ=0 EndX=-3.8 EndY=0 EndZ=0
    g3: LineSegment StartX=-3.8 StartY=0 StartZ=0 EndX=-3.8 EndY=8 EndZ=0
  constraints (11):
    c: Coincident(g0,g1)
    c: Coincident(g1,g2)
    c: Coincident(g2,g3)
    c: Coincident(g3,g0)
    c: Horizontal(g2)
    c: Vertical(g1)
    c: Vertical(g3)
    c: Symmetric(g0,g0,g-2)
    c: PointOnObject(g2,g-1)
    c: PointOnObject(g0,g-3)
    c: DistanceX(g0,g0) = 7.6
FEATURE [PartDesign::Pocket] Pocket017
  BaseFeature = -> Pad027
  Length = 7
  Length2 = 100
  Placement = pos=(0,0,0) rot=(0.57735,0.57735,0.57735;2.0944rad)
  Profile = -> Sketch049
  Type = 0
FEATURE [Sketcher::SketchObject] Sketch050
  ExternalGeometry = -> [Pocket017]
  FullyConstrained = true
  MapMode = 5
  Placement = pos=(-4e-15,-8,1.8e-15) rot=(-0.57735,-0.57735,0.57735;4.18879rad)
  Support = -> [Pocket017]
  sketch-geometry (4):
    g0: LineSegment StartX=-3 StartY=12 StartZ=0 EndX=0 EndY=12 EndZ=0
    g1: LineSegment StartX=0 StartY=12 StartZ=0 EndX=0 EndY=6 EndZ=0
    g2: LineSegment StartX=0 StartY=6 StartZ=0 EndX=-3 EndY=6 EndZ=0
    g3: LineSegment StartX=-3 StartY=6 StartZ=0 EndX=-3 EndY=12 EndZ=0
  constraints (12):
    c: Coincident(g0,g1)
    c: Coincident(g1,g2)
    c: Coincident(g2,g3)
    c: Coincident(g3,g0)
    c: Horizontal(g0)
    c: Horizontal(g2)
    c: Vertical(g1)
    c: Vertical(g3)
    c: PointOnObject(g0,g-3)
    c: PointOnObject(g1,g-2)
    c: DistanceX(g0,g0) = 3
    c: DistanceY(g3,g3) = 6
FEATURE [PartDesign::Pocket] Pocket018
  BaseFeature = -> Pocket017
  Length = 5
  Length2 = 100
  Placement = pos=(0,0,0) rot=(0.57735,0.57735,0.57735;2.0944rad)
  Profile = -> Sketch050
  Type = 1
FEATURE [Sketcher::SketchObject] Sketch051
  FullyConstrained = true
  MapMode = 5
  Placement = pos=(0,0,0) rot=(0.57735,0.57735,0.57735;2.0944rad)
  Support = -> [YZ_Plane006]
  sketch-geometry (4):
    g0: LineSegment StartX=-10 StartY=3.2 StartZ=0 EndX=10 EndY=3.2 EndZ=0
    g1: LineSegment StartX=10 StartY=3.2 StartZ=0 EndX=10 EndY=-3.2 EndZ=0
    g2: LineSegment StartX=10 StartY=-3.2 StartZ=0 EndX=-10 EndY=-3.2 EndZ=0
    g3: LineSegment StartX=-10 StartY=-3.2 StartZ=0 EndX=-10 EndY=3.2 EndZ=0
  constraints (10):
    c: Coincident(g0,g1)
    c: Coincident(g1,g2)
    c: Coincident(g2,g3)
    c: Coincident(g3,g0)
    c: Horizontal(g2)
    c: Vertical(g3)
    c: Symmetric(g1,g0,g-1)
    c: Symmetric(g0,g0,g-2)
    c: DistanceX(g0,g0) = 20
    c: DistanceY(g1,g1) = 6.4
FEATURE [PartDesign::Pad] Pad028
  Direction = (1,1,1)
  Length = 0.4
  Length2 = 100
  Placement = pos=(0,0,0) rot=(0.57735,0.57735,0.57735;2.0944rad)
  Profile = -> Sketch051
  Type = 0
FEATURE [Sketcher::SketchObject] Sketch052
  ExternalGeometry = -> [Pad028]
  FullyConstrained = true
  MapMode = 5
  Placement = pos=(0,0,0) rot=(0.57735,0.57735,-0.57735;4.18879rad)
  Support = -> [Pad028]
  sketch-geometry (4):
    g0: LineSegment StartX=-3 StartY=2.8 StartZ=0 EndX=3 EndY=2.8 EndZ=0
    g1: LineSegment StartX=3 StartY=2.8 StartZ=0 EndX=3 EndY=-2.8 EndZ=0
    g2: LineSegment StartX=3 StartY=-2.8 StartZ=0 EndX=-3 EndY=-2.8 EndZ=0
    g3: LineSegment StartX=-3 StartY=-2.8 StartZ=0 EndX=-3 EndY=2.8 EndZ=0
  constraints (11):
    c: Coincident(g0,g1)
    c: Coincident(g1,g2)
    c: Coincident(g2,g3)
    c: Coincident(g3,g0)
    c: Horizontal(g2)
    c: Vertical(g3)
    c: Symmetric(g0,g0,g-2)
    c: DistanceX(g0,g0) = 6
    c: Symmetric(g1,g0,g-1)
    c: DistanceY(g1,g1) = 5.6
    c: DistanceY(g-4,g-3) = 6.4
FEATURE [PartDesign::Pad] Pad029
  BaseFeature = -> Pad028
  Direction = (1,1,1)
  Length = 4
  Length2 = 100
  Placement = pos=(0,0,0) rot=(0.57735,0.57735,0.57735;2.0944rad)
  Profile = -> Sketch052
  Type = 0
FEATURE [PartDesign::Body] Body006  label="Button-Enter"
  Group = -> [Sketch051,Pad028,Sketch052,Pad029]
  Origin = -> Origin006
  Placement = pos=(-46.2,-30.1,14.1) rot=(0,0,1;0rad)
  Tip = -> Pad029
FEATURE [Sketcher::SketchObject] Sketch053
  FullyConstrained = true
  MapMode = 5
  Placement = pos=(0,0,0) rot=(0.57735,0.57735,0.57735;2.0944rad)
  Support = -> [YZ_Plane007]
  sketch-geometry (4):
    g0: LineSegment StartX=-9.7 StartY=2.7 StartZ=0 EndX=9.7 EndY=2.7 EndZ=0
    g1: LineSegment StartX=9.7 StartY=2.7 StartZ=0 EndX=9.7 EndY=-2.7 EndZ=0
    g2: LineSegment StartX=9.7 StartY=-2.7 StartZ=0 EndX=-9.7 EndY=-2.7 EndZ=0
    g3: LineSegment StartX=-9.7 StartY=-2.7 StartZ=0 EndX=-9.7 EndY=2.7 EndZ=0
  constraints (10):
    c: Coincident(g0,g1)
    c: Coincident(g1,g2)
    c: Coincident(g2,g3)
    c: Coincident(g3,g0)
    c: Horizontal(g2)
    c: Vertical(g3)
    c: Symmetric(g0,g0,g-2)
    c: Symmetric(g1,g0,g-1)
    c: DistanceY(g3,g3) = 5.4
    c: DistanceX(g2,g2) = 19.4
FEATURE [PartDesign::Pad] Pad030
  Direction = (1,1,1)
  Length = 0.4
  Length2 = 100
  Placement = pos=(0,0,0) rot=(0.57735,0.57735,0.57735;2.0944rad)
  Profile = -> Sketch053
  Type = 0
FEATURE [Sketcher::SketchObject] Sketch054
  ExternalGeometry = -> [Pad030]
  FullyConstrained = true
  MapMode = 5
  Placement = pos=(0.4,-1e-16,1e-16) rot=(0.57735,0.57735,0.57735;2.0944rad)
  Support = -> [Pad030]
  sketch-geometry (4):
    g0: LineSegment StartX=-3.5 StartY=2.4 StartZ=0 EndX=3.5 EndY=2.4 EndZ=0
    g1: LineSegment StartX=3.5 StartY=2.4 StartZ=0 EndX=3.5 EndY=-2.4 EndZ=0
    g2: LineSegment StartX=3.5 StartY=-2.4 StartZ=0 EndX=-3.5 EndY=-2.4 EndZ=0
    g3: LineSegment StartX=-3.5 StartY=-2.4 StartZ=0 EndX=-3.5 EndY=2.4 EndZ=0
  constraints (11):
    c: Coincident(g0,g1)
    c: Coincident(g1,g2)
    c: Coincident(g2,g3)
    c: Coincident(g3,g0)
    c: Horizontal(g2)
    c: Vertical(g3)
    c: Symmetric(g0,g0,g-2)
    c: DistanceX(g0,g0) = 7
    c: Symmetric(g0,g1,g-1)
    c: DistanceY(g1,g1) = 4.8
    c: DistanceY(g-4,g-3) = 5.4
FEATURE [PartDesign::Pad] Pad031
  BaseFeature = -> Pad030
  Direction = (1,1,1)
  Length = 4
  Length2 = 100
  Placement = pos=(0,0,0) rot=(0.57735,0.57735,0.57735;2.0944rad)
  Profile = -> Sketch054
  Type = 0
FEATURE [PartDesign::Body] Body007  label="Button-Power"
  Group = -> [Sketch053,Pad030,Sketch054,Pad031]
  Origin = -> Origin007
  Placement = pos=(46.8,-38.6,-1.95) rot=(0,0,1;0rad)
  Tip = -> Pad031
FEATURE [Sketcher::SketchObject] Sketch055
  ExternalGeometry = -> [ShapeBinder003]
  FullyConstrained = true
  MapMode = 5
  Placement = pos=(-32.7,0,0) rot=(0.57735,0.57735,0.57735;2.0944rad)
  Support = -> [Pocket001]
  sketch-geometry (14):
    g0: LineSegment StartX=-49.9 StartY=-13.6743 StartZ=0 EndX=-47 EndY=-15.3486 EndZ=0
    g1: LineSegment StartX=-47 StartY=-15.3486 StartZ=0 EndX=-44.1 EndY=-13.6743 EndZ=0
    g2: LineSegment StartX=-44.1 StartY=-13.6743 StartZ=0 EndX=-44.1 EndY=-10.3257 EndZ=0
    g3: LineSegment StartX=-44.1 StartY=-10.3257 StartZ=0 EndX=-47 EndY=-8.65137 EndZ=0
    g4: LineSegment StartX=-47 StartY=-8.65137 StartZ=0 EndX=-49.9 EndY=-10.3257 EndZ=0
    g5: LineSegment StartX=-49.9 StartY=-10.3257 StartZ=0 EndX=-49.9 EndY=-13.6743 EndZ=0
    g6: Circle CenterX=-47 CenterY=-12 CenterZ=0 NormalX=0 NormalY=0 NormalZ=1 AngleXU=0 Radius=3.34863
    g7: LineSegment StartX=48 StartY=-15.3486 StartZ=0 EndX=50.9 EndY=-13.6743 EndZ=0
    g8: LineSegment StartX=50.9 StartY=-13.6743 StartZ=0 EndX=50.9 EndY=-10.3257 EndZ=0
    g9: LineSegment StartX=50.9 StartY=-10.3257 StartZ=0 EndX=48 EndY=-8.65137 EndZ=0
    g10: LineSegment StartX=48 StartY=-8.65137 StartZ=0 EndX=45.1 EndY=-10.3257 EndZ=0
    g11: LineSegment StartX=45.1 StartY=-10.3257 StartZ=0 EndX=45.1 EndY=-13.6743 EndZ=0
    g12: LineSegment StartX=45.1 StartY=-13.6743 StartZ=0 EndX=48 EndY=-15.3486 EndZ=0
    g13: Circle CenterX=48 CenterY=-12 CenterZ=0 NormalX=0 NormalY=0 NormalZ=1 AngleXU=0 Radius=3.34863
  constraints (32):
    c: Coincident(g0,g1)
    c: Coincident(g1,g2)
    c: Coincident(g2,g3)
    c: Coincident(g3,g4)
    c: Coincident(g4,g5)
    c: Coincident(g5,g0)
    c: Equal(g0, g1-g5) x5
    c: PointOnObject(g0,g6)
    c: PointOnObject(g1,g6)
    c: PointOnObject(g2,g6)
    c: PointOnObject(g3,g6)
    c: PointOnObject(g4,g6)
    c: PointOnObject(g5,g6)
    c: Coincident(g7,g8)
    c: Coincident(g8,g9)
    c: Coincident(g9,g10)
    c: Coincident(g10,g11)
    c: Coincident(g11,g12)
    c: Coincident(g12,g7)
    c: Equal(g7, g8-g12) x5
    c: PointOnObject(g7,g13)
    c: PointOnObject(g8,g13)
    c: PointOnObject(g9,g13)
    c: PointOnObject(g10,g13)
    c: PointOnObject(g11,g13)
    c: PointOnObject(g12,g13)
    c: Equal(g6,g13)
    c: Symmetric(g-6,g-5,g13)
    c: Vertical(g13,g9)
    c: Symmetric(g-3,g-4,g6)
    c: Vertical(g6,g3)
    c: DistanceX(g0,g1) = 5.8
FEATURE [PartDesign::Pocket] Pocket019
  BaseFeature = -> Pocket001
  Length = 3
  Length2 = 100
  Profile = -> Sketch055
  Type = 0
FEATURE [Sketcher::SketchObject] Sketch056
  ExternalGeometry = -> [ShapeBinder003]
  FullyConstrained = true
  MapMode = 5
  Placement = pos=(33.7,0,0) rot=(0.57735,-0.57735,-0.57735;2.0944rad)
  Support = -> [Pocket019]
  sketch-geometry (14):
    g0: LineSegment StartX=47 StartY=-15.3486 StartZ=0 EndX=49.9 EndY=-13.6743 EndZ=0
    g1: LineSegment StartX=49.9 StartY=-13.6743 StartZ=0 EndX=49.9 EndY=-10.3257 EndZ=0
    g2: LineSegment StartX=49.9 StartY=-10.3257 StartZ=0 EndX=47 EndY=-8.65137 EndZ=0
    g3: LineSegment StartX=47 StartY=-8.65137 StartZ=0 EndX=44.1 EndY=-10.3257 EndZ=0
    g4: LineSegment StartX=44.1 StartY=-10.3257 StartZ=0 EndX=44.1 EndY=-13.6743 EndZ=0
    g5: LineSegment StartX=44.1 StartY=-13.6743 StartZ=0 EndX=47 EndY=-15.3486 EndZ=0
    g6: Circle CenterX=47 CenterY=-12 CenterZ=0 NormalX=0 NormalY=0 NormalZ=1 AngleXU=0 Radius=3.34863
    g7: LineSegment StartX=-45.1 StartY=-13.6743 StartZ=0 EndX=-45.1 EndY=-10.3257 EndZ=0
    g8: LineSegment StartX=-45.1 StartY=-10.3257 StartZ=0 EndX=-48 EndY=-8.65137 EndZ=0
    g9: LineSegment StartX=-48 StartY=-8.65137 StartZ=0 EndX=-50.9 EndY=-10.3257 EndZ=0
    g10: LineSegment StartX=-50.9 StartY=-10.3257 StartZ=0 EndX=-50.9 EndY=-13.6743 EndZ=0
    g11: LineSegment StartX=-50.9 StartY=-13.6743 StartZ=0 EndX=-48 EndY=-15.3486 EndZ=0
    g12: LineSegment StartX=-48 StartY=-15.3486 StartZ=0 EndX=-45.1 EndY=-13.6743 EndZ=0
    g13: Circle CenterX=-48 CenterY=-12 CenterZ=0 NormalX=0 NormalY=0 NormalZ=1 AngleXU=0 Radius=3.34863
  constraints (32):
    c: Coincident(g0,g1)
    c: Coincident(g1,g2)
    c: Coincident(g2,g3)
    c: Coincident(g3,g4)
    c: Coincident(g4,g5)
    c: Coincident(g5,g0)
    c: Equal(g0, g1-g5) x5
    c: PointOnObject(g0,g6)
    c: PointOnObject(g1,g6)
    c: PointOnObject(g2,g6)
    c: PointOnObject(g3,g6)
    c: PointOnObject(g4,g6)
    c: PointOnObject(g5,g6)
    c: Coincident(g7,g8)
    c: Coincident(g8,g9)
    c: Coincident(g9,g10)
    c: Coincident(g10,g11)
    c: Coincident(g11,g12)
    c: Coincident(g12,g7)
    c: Equal(g7, g8-g12) x5
    c: PointOnObject(g7,g13)
    c: PointOnObject(g8,g13)
    c: PointOnObject(g9,g13)
    c: PointOnObject(g10,g13)
    c: PointOnObject(g11,g13)
    c: PointOnObject(g12,g13)
    c: Equal(g13,g6)
    c: Symmetric(g-5,g-6,g6)
    c: Vertical(g6,g2)
    c: DistanceX(g4,g0) = 5.8
    c: Symmetric(g-3,g-4,g13)
    c: Vertical(g8,g13)
FEATURE [PartDesign::Pocket] Pocket020
  BaseFeature = -> Pocket019
  Length = 3
  Length2 = 100
  Profile = -> Sketch056
  Type = 0
FEATURE [PartDesign::Body] Body002  label="Base"
  Group = -> [ShapeBinder001,ShapeBinder003,Sketch017,Pad015,Sketch018,Pocket,Sketch019,Pad016,Sketch020,Pad017,Sketch021,Pocket001,Sketch055,Pocket019,Sketch056,Pocket020]
  Origin = -> Origin002
  Tip = -> Pocket020
FEATURE [Sketcher::SketchObject] Sketch057
  FullyConstrained = true
  MapMode = 5
  Placement = pos=(0,-53,0) rot=(1,0,0;1.5708rad)
  Support = -> [Chamfer001]
  sketch-geometry (2):
    g0: Circle CenterX=25 CenterY=-14 CenterZ=0 NormalX=0 NormalY=0 NormalZ=1 AngleXU=0 Radius=1.2
    g1: Circle CenterX=30 CenterY=-14 CenterZ=0 NormalX=0 NormalY=0 NormalZ=1 AngleXU=0 Radius=1.2
  constraints (6):
    c: DistanceX(g-1,g1) = 30
    c: Equal(g1,g0)
    c: Radius(g1) = 1.2
    c: Horizontal(g1,g0)
    c: DistanceX(g0,g1) = 5
    c: DistanceY(g1,g-1) = 14
FEATURE [PartDesign::Pocket] Pocket021
  BaseFeature = -> Chamfer001
  Length = 3
  Length2 = 100
  Profile = -> Sketch057
  Type = 0
FEATURE [Sketcher::SketchObject] Sketch058
  ExternalGeometry = -> [Pocket012]
  FullyConstrained = true
  MapMode = 5
  Placement = pos=(0,0,14.6) rot=(1,0,0;3.14159rad)
  Support = -> [Pocket012]
  sketch-geometry (1):
    g0: Circle CenterX=0 CenterY=28.75 CenterZ=0 NormalX=0 NormalY=0 NormalZ=1 AngleXU=0 Radius=2.2
  constraints (3):
    c: PointOnObject(g0,g-2)
    c: DistanceY(g0,g-3) = 5.75
    c: Radius(g0) = 2.2
FEATURE [PartDesign::Pocket] Pocket022
  BaseFeature = -> Pocket012
  Length = 6
  Length2 = 100
  Profile = -> Sketch058
  Type = 0
FEATURE [PartDesign::Chamfer] Chamfer002
  Angle = 45
  Base = -> Pocket022 [Edge42,Edge40,Edge41,Edge33,Face5,Edge31,Edge32,Edge39,Edge37,Edge38,Edge36,Edge34,Edge35]
  BaseFeature = -> Pocket022
  ChamferType = 0
  FlipDirection = false
  Size = 0.6
  Size2 = 1
  SupportTransform = false
FEATURE [PartDesign::Body] Body004  label="Button-Cross"
  Group = -> [ShapeBinder006,Sketch039,Pad025,Sketch041,Pad026,Sketch042,Pocket012,Sketch058,Pocket022,Chamfer002]
  Origin = -> Origin004
  Tip = -> Chamfer002
FEATURE [Sketcher::SketchObject] Sketch059
  ExternalGeometry = -> [Pocket021]
  FullyConstrained = true
  MapMode = 5
  Placement = pos=(-48.5,0,0) rot=(0.57735,-0.57735,-0.57735;2.0944rad)
  Support = -> [Pocket021]
  sketch-geometry (12):
    g0: LineSegment StartX=-44.2 StartY=21.6 StartZ=0 EndX=-34.8 EndY=21.6 EndZ=0
    g1: LineSegment StartX=-18 StartY=4.4 StartZ=0 EndX=-18 EndY=1.4 EndZ=0
    g2: LineSegment StartX=-21.4 StartY=-2 StartZ=0 EndX=-44.2 EndY=-2 EndZ=0
    g3: LineSegment StartX=-47.6 StartY=1.4 StartZ=0 EndX=-47.6 EndY=18.2 EndZ=0
    g4: LineSegment StartX=-21.4 StartY=7.8 StartZ=0 EndX=-28 EndY=7.8 EndZ=0
    g5: LineSegment StartX=-31.4 StartY=11.2 StartZ=0 EndX=-31.4 EndY=18.2 EndZ=0
    g6: ArcOfCircle CenterX=-28 CenterY=11.2 CenterZ=0 NormalX=0 NormalY=0 NormalZ=1 AngleXU=0 Radius=3.4 StartAngle=3.14159 EndAngle=4.71239
    g7: ArcOfCircle CenterX=-34.8 CenterY=18.2 CenterZ=0 NormalX=0 NormalY=0 NormalZ=1 AngleXU=0 Radius=3.4 StartAngle=0 EndAngle=1.5708
    g8: ArcOfCircle CenterX=-44.2 CenterY=18.2 CenterZ=0 NormalX=0 NormalY=0 NormalZ=1 AngleXU=0 Radius=3.4 StartAngle=1.5708 EndAngle=3.14159
    g9: ArcOfCircle CenterX=-44.2 CenterY=1.4 CenterZ=0 NormalX=0 NormalY=0 NormalZ=1 AngleXU=0 Radius=3.4 StartAngle=3.14159 EndAngle=4.71239
    g10: ArcOfCircle CenterX=-21.4 CenterY=1.4 CenterZ=0 NormalX=0 NormalY=0 NormalZ=1 AngleXU=0 Radius=3.4 StartAngle=4.71239 EndAngle=6.28319
    g11: ArcOfCircle CenterX=-21.4 CenterY=4.4 CenterZ=0 NormalX=0 NormalY=0 NormalZ=1 AngleXU=0 Radius=3.4 StartAngle=0 EndAngle=1.5708
  constraints (27):
    c: Horizontal(g0)
    c: Horizontal(g2)
    c: Vertical(g1)
    c: Vertical(g3)
    c: Horizontal(g4)
    c: Vertical(g5)
    c: Tangent(g4,g6) = 1.5708
    c: Tangent(g5,g6) = 1.5708
    c: Tangent(g5,g7) = -1.5708
    c: Tangent(g0,g8) = 1.5708
    c: Tangent(g3,g8) = 1.5708
    c: Tangent(g2,g9) = 1.5708
    c: Tangent(g3,g9) = 1.5708
    c: Tangent(g1,g10) = 1.5708
    c: Tangent(g2,g10) = 1.5708
    c: Tangent(g1,g11) = 1.5708
    c: Tangent(g4,g11) = -1.5708
    c: Equal(g7,g6)
    c: Equal(g6,g11)
    c: Equal(g10,g9)
    c: Radius(g10) = 3.4
    c: Coincident(g-3,g8)
    c: Coincident(g-4,g10)
    c: Coincident(g7,g-5)
    c: Coincident(g-6,g11)
    c: Coincident(g0,g7)
    c: Vertical(g7,g0)
FEATURE [PartDesign::Pocket] Pocket023
  BaseFeature = -> Pocket021
  Length = 0.6
  Length2 = 100
  Profile = -> Sketch059
  Type = 0
FEATURE [PartDesign::Fillet] Fillet
  Base = -> Pocket023 [Edge136,Edge135,Edge134,Edge133,Edge132,Edge131,Edge130,Edge129,Edge128,Edge139,Edge138,Edge137]
  BaseFeature = -> Pocket023
  Radius = 0.4
  SupportTransform = false
FEATURE [PartDesign::Body] Body003  label="Cover"
  Group = -> [ShapeBinder002,ShapeBinder004,ShapeBinder007,Sketch023,Pad018,Sketch024,Pocket003,Sketch025,Pocket004,Sketch026,Pocket005,Sketch027,Pad019,Sketch028,Pad020,Sketch029,Pocket006,Sketch030,Pocket007,Sketch031,Pocket008,Sketch032,Pocket009,Sketch033,Pocket010,Sketch040,Pocket011,Sketch043,Pocket013,Sketch044,Pocket014,Sketch045,Pocket015,Chamfer,Sketch047,Pocket016,Chamfer001,Sketch057,Pocket021,+3 more]
  Origin = -> Origin003
  Tip = -> Fillet
FEATURE [Mesh::Feature] Mesh  label="Base (Meshed)"
FEATURE [Mesh::Feature] Mesh002  label="Button-Cross (Meshed)"
FEATURE [Mesh::Feature] Mesh006  label="Cover (Meshed)"
FEATURE [Sketcher::SketchObject] Sketch060
  ExternalGeometry = -> [Pocket018]
  FullyConstrained = true
  MapMode = 5
  Placement = pos=(1.1e-15,3.8,-2e-16) rot=(-0.57735,-0.57735,0.57735;4.18879rad)
  Support = -> [Pocket018]
  sketch-geometry (4):
    g0: LineSegment StartX=-8 StartY=12 StartZ=0 EndX=-4.6 EndY=12 EndZ=0
    g1: LineSegment StartX=-4.6 StartY=12 StartZ=0 EndX=-4.6 EndY=10 EndZ=0
    g2: LineSegment StartX=-4.6 StartY=10 StartZ=0 EndX=-8 EndY=10 EndZ=0
    g3: LineSegment StartX=-8 StartY=10 StartZ=0 EndX=-8 EndY=12 EndZ=0
  constraints (11):
    c: Coincident(g0,g1)
    c: Coincident(g1,g2)
    c: Coincident(g2,g3)
    c: Coincident(g3,g0)
    c: Horizontal(g0)
    c: Horizontal(g2)
    c: Vertical(g1)
    c: Vertical(g3)
    c: Coincident(g0,g-3)
    c: DistanceX(g0,g0) = 3.4
    c: DistanceY(g1,g1) = 2
FEATURE [PartDesign::Pad] Pad032
  BaseFeature = -> Pocket018
  Direction = (1,1,1)
  Length = 9
  Length2 = 100
  Placement = pos=(0,0,0) rot=(0.57735,0.57735,0.57735;2.0944rad)
  Profile = -> Sketch060
  Type = 0
FEATURE [PartDesign::Body] Body005  label="Button-Guide"
  Group = -> [Sketch048,Pad027,Sketch049,Pocket017,Sketch050,Pocket018,Sketch060,Pad032]
  Origin = -> Origin005
  Placement = pos=(-45.5,-30.1,10.6) rot=(0,0,1;0rad)
  Tip = -> Pad032
FEATURE [Mesh::Feature] Mesh007  label="Button-Guide (Meshed)"
FEATURE [Mesh::Feature] Mesh008  label="Button-Enter (Meshed)"
FEATURE [Mesh::Feature] Mesh009  label="Button-Power (Meshed)"
